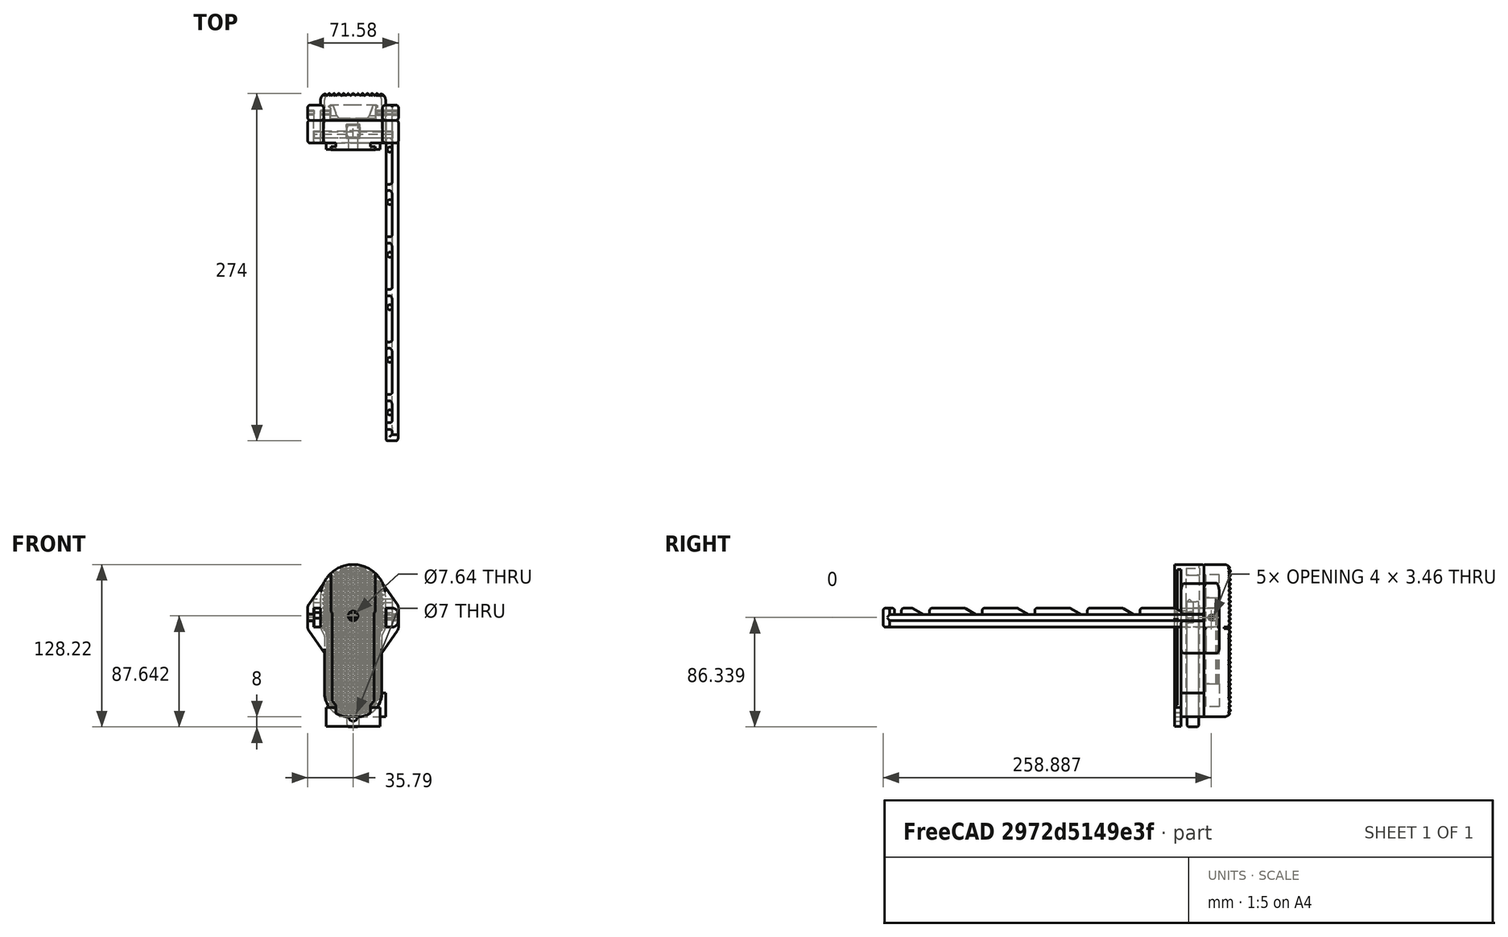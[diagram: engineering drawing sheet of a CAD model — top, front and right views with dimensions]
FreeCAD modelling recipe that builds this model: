
FCSTD DOCUMENT  (FreeCAD 0.19R24291 (Git))
Label: TelescopingButtExtensionPlasticArmsV3
License: All rights reserved
LicenseURL: http://en.wikipedia.org/wiki/All_rights_reserved
objects: Sketcher::SketchObject×35, PartDesign::Pocket×17, PartDesign::Pad×15, PartDesign::Fillet×10, PartDesign::Body×9, Spreadsheet::Sheet×5, PartDesign::Mirrored×4, PartDesign::LinearPattern×3, App::Part×3, Part::Mirroring×2, PartDesign::SubtractivePipe×1, PartDesign::AdditivePipe×1, PartDesign::Groove×1, PartDesign::Chamfer×1
note: 145 computed .brp shape members not serialized (recipe doc carries the construction recipe); baked Part::Feature solids carry a one-line shape summary decoded from their .brp

FEATURE [Spreadsheet::Sheet] Spreadsheet  label="P90Measurements"
  cells = A1=ButtDovetail; D1=Overall; G1=ButtPad; I1=Reference Point; J1=Bottom of pad, just at base of dovetail body; L1=SpaceForTelescopingBar; M1(SpaceForTelescopingBar)==0.584"; A2=DovetailHeight; B2(DovetailHeight)==5mm; D2=ButtOverallHeight; E2(ButtOverallHeight)==4.733"; G2=PadWidestWidth; H2(PadWidestWidth)==2.017"; A3=DovetailBodyWidth; B3(DovetailBodyWidth)==28mm; D3=PadBCGHoleFromReferencePoint; E3(PadBCGHoleFromReferencePoint)==2.997"; G3=PadThinnestWidth; H3(PadThinnestWidth)==1.772"; A4=DovetailLedgeHeight; B4(DovetailLedgeHeight)==2.5mm; D4=PadBCGHoleDiameter; E4(PadBCGHoleDiameter)==0.277"; G4=PadWidestWidthInnerShoulderDistanceFromReferencePoint; H4(PadWidestWidthInnerShoulderDistanceFromReferencePoint)==2.532"; A5=DovetailLedgeWidestWidth; B5(DovetailLedgeWidestWidth)==35.5mm; D5=PadBCGHoleDepth; E5(PadBCGHoleDepth)==0.375"; G5=PadWidestWidthOuterShoulderDistanceFromReferencePoint; H5(PadWidestWidthOuterShoulderDistanceFromReferencePoint)==2.785"; A6=DovetailLedgeMiddleWidth; B6(DovetailLedgeMiddleWidth)==1.32"; G6=PadBottomWidth; H6(PadBottomWidth)==0.3"; A7=DovetailMiddleWidthInsideShoulderDistanceFromReferencePoint; B7(DovetailMiddleWidthInsideShoulderDistanceFromReferencePoint)==0.37"; A8=DovetailMiddleWidthOutsideShoulderDistanceFromReferencePoint; B8(DovetailMiddleWidthOutsideShoulderDistanceFromReferencePoint)==0.484"; A9=DovetailBottobBodyBevelDistanceFromReferencePoint; B9(DovetailBottobBodyBevelDistanceFromReferencePoint)==0.154"; A10=DovetailWidestLedgeStartingPointFromReferencePoint; B10(DovetailWidestLedgeStartingPointFromReferencePoint)==3.222"
FEATURE [Spreadsheet::Sheet] Spreadsheet001  label="ProjectSettings"
  cells = A1=Tolerance; A2=LooseTolerance; B2(LooseTolerance)==0.3mm; C2=SpringMaxHeight; D2(SpringMaxHeight)==20mm; E2=CrosspinWidth; F2(CrosspinWidth)==4mm; G2=EndcapScrewBodyDiameter; H2(EndcapScrewBodyDiameter)==4mm; I2=LengthFromButtToChargingHandleShelf; J2(LengthFromButtToChargingHandleShelf)==310mm; K2=AdditionalPrinterTolerance; L2(AdditionalPrinterTolerance)==0mm; A3=TightTolerance; B3(TightTolerance)==0.1mm + AdditionalPrinterTolerance; C3=TelescopingPadOAL; D3(TelescopingPadOAL)==TelescopingBarInsertDepth + TelescopingButtThickness; E3=CrosspinHeight; F3(CrosspinHeight)==BarHeight / 3; G3=EndcapScrewHeadDiameter; H3(EndcapScrewHeadDiameter)==6mm; K3=SupportGap; L3(SupportGap)==0.16mm; A4=WallThickness; B4(WallThickness)==4mm; C4=StandardFillet; D4(StandardFillet)==2mm; E4=CrosspinLength; G4=EndcapNutHeight; H4(EndcapNutHeight)==0.273"; A5=LockingButtonWidth; B5(LockingButtonWidth)==10mm; C5=LockingPinWidth; D5(LockingPinWidth)==0.1875"; E5=ButtonActuationDistance; F5(ButtonActuationDistance)==CrosspinHeight * 2; G5=EndcapNutThickness; H5(EndcapNutThickness)==0.121"; A6=LockingButtonHeight; B6(LockingButtonHeight)==10mm; C6=LockingPinHeight; D6(LockingPinHeight)==BarHeight / 3 - LooseTolerance * 2; G6=EndcapSectionOnBarLength; H6(EndcapSectionOnBarLength)==15mm; A7=LockingButtonLength; B7(LockingButtonLength)==60mm; C7=LockingPinLength; D7(LockingPinLength)==40mm; G7=EndcapSectionHangingOffOfBarLength; H7(EndcapSectionHangingOffOfBarLength)==WallThickness; A8=LockingButtonHoleDepth; B8(LockingButtonHoleDepth)==<<P90Measurements>>.PadWidestWidthOuterShoulderDistanceFromReferencePoint + BarThickness + LockingPinHeight * 3 + SpringMaxHeight; C8=BarThickness; D8(BarThickness)==5mm; G8=ScrewCountersinkDepth; H8(ScrewCountersinkDepth)==0.089"; A9=LockingButtonActuationDistance; B9(LockingButtonActuationDistance)==6mm; C9=BarHeight; D9(BarHeight)==15mm; G9=EndcapScrewThreadHeight; H9(EndcapScrewThreadHeight)==8mm; A10=LockingBodyLength; B10(LockingBodyLength)==WallThickness * 2 + LockingButtonHeight; C10=BarLength; D10(BarLength)==265mm; A11=TelescopingPadComfortFilletRadius; B11(TelescopingPadComfortFilletRadius)==5mm; C11=BarNumberOfKnotches; D11(BarNumberOfKnotches)=6; C12=TelescopingBarInsertDepth; D12(TelescopingBarInsertDepth)==WallThickness * 2 + CrosspinWidth; A13=ScallopRadius; B13(ScallopRadius)==1.5mm; C13=TelescopingButtThickness; D13(TelescopingButtThickness)==10mm; A14=DistanceBetweenScallops; B14(DistanceBetweenScallops)==0.25mm; C14=BarDistanceBetweenKnotches; D14(BarDistanceBetweenKnotches)=; C15=BarLastKnotchLocationFromOrigin; D15(BarLastKnotchLocationFromOrigin)==BarLength - EndcapSectionOnBarLength - WallThickness; A16=PaperworkLidNubWidth; B16(PaperworkLidNubWidth)==2mm; C16=BarOccupiedLength; D16(BarOccupiedLength)==WallThickness * 4 + LockingButtonHeight + CrosspinWidth; A17=PaperworkLidNubHeight; B17(PaperworkLidNubHeight)==1.5mm; C17=BarUnoccupiedLength; D17(BarUnoccupiedLength)==BarLength - BarOccupiedLength; A18=PaperworkLidWallThickness; B18(PaperworkLidWallThickness)==2mm; C18=BarRackAngle; D18(BarRackAngle)=150; A19=PaperworkLidFingerHoleDiameter; B19(PaperworkLidFingerHoleDiameter)==20mm; C19=BarRackFillet; D19(BarRackFillet)==2mm; A20=PaperworkLipTabWallFilletRadius; B20(PaperworkLipTabWallFilletRadius)==4mm; C20=BarFillet; D20(BarFillet)==2mm; A21=PaperwokLipInteriorWallAngle; B21(PaperwokLipInteriorWallAngle)=110; C21=BarRackStartOffset; D21(BarRackStartOffset)==TelescopingBarInsertDepth + WallThickness + LockingButtonWidth / 2; A22=PaperworklidbaseThickness; B22(PaperworklidbaseThickness)==1.5mm; C22=BarRackEndoffset; D22(BarRackEndoffset)==WallThickness * 2 + LockingPinWidth + BarThickness; C23=BarRackL:ength; D23(BarRackLength)==13.6mm; A24=LockingButtonHoleClearanceForChamfer; B24(LockingButtonHoleClearanceForChamfer)==min(LockingButtonWidth; LockingButtonHeight) * 9 / 20; C24=BarEndcapThickness; D24(BarEndcapThickness)==BarThickness; A25=LockingPinPocketOverhangCompensationDistance; B25(LockingPinPocketOverhangCompensationDistance)==1.5mm; C25=PadCrosspinLength; D25(PadCrosspinLength)==17mm; C26=BCGInsertOffset; D26(BCGInsertOffset)==5mm; A27=LockingBodyPadThickness; B27(LockingBodyPadThickness)==WallThickness * 2 + LockingButtonHeight; C27=BCGWidth; D27(BCGWidth)==42.5mm; C28=BcgEndHeight; D28(BcgEndHeight)==15mm
FEATURE [Sketcher::SketchObject] Sketch  label="DovetailBodySketch"
  FullyConstrained = true
  MapMode = 5
  Placement = pos=(0,0,0) rot=(1,0,0;1.5708rad)
  Support = -> [XZ_Plane]
  expr: Constraints[9] = <<P90Measurements>>.ButtOverallHeight
  expr: Constraints[10] = <<P90Measurements>>.DovetailBodyWidth - <<ProjectSettings>>.LooseTolerance * 2
  sketch-geometry (4):
    g0: LineSegment StartX=-13.7 StartY=120.218 StartZ=0 EndX=13.7 EndY=120.218 EndZ=0
    g1: LineSegment StartX=13.7 StartY=120.218 StartZ=0 EndX=13.7 EndY=0 EndZ=0
    g2: LineSegment StartX=13.7 StartY=0 StartZ=0 EndX=-13.7 EndY=0 EndZ=0
    g3: LineSegment StartX=-13.7 StartY=0 StartZ=0 EndX=-13.7 EndY=120.218 EndZ=0
  constraints (11):
    c: Coincident(g0,g1)
    c: Coincident(g1,g2)
    c: Coincident(g2,g3)
    c: Coincident(g3,g0)
    c: Horizontal(g0)
    c: Vertical(g1)
    c: Vertical(g3)
    c: PointOnObject(g1,g-1)
    c: Symmetric(g1,g2,g-2)
    c: DistanceY(g1,g1) = 120.218
    c: DistanceX(g0,g0) = 27.4
FEATURE [PartDesign::Pad] Pad  label="DovetailBodyPad"
  Direction = (1,1,1)
  Length = 5.2
  Length2 = 100
  Placement = pos=(0,0,0) rot=(1,0,0;1.5708rad)
  Profile = -> Sketch
  Type = 0
  expr: Length = <<P90Measurements>>.DovetailHeight + <<ProjectSettings>>.TightTolerance * 2
FEATURE [Sketcher::SketchObject] Sketch001  label="DovetailLedgeSketch"
  AttachmentOffset = pos=(0,0,5.2) rot=(0,0,1;0rad)
  FullyConstrained = true
  MapMode = 5
  Placement = pos=(0,-5.2,-1.2e-15) rot=(1,0,0;1.5708rad)
  Support = -> [XZ_Plane]
  expr: Constraints[9] = <<P90Measurements>>.ButtOverallHeight
  expr: Constraints[10] = <<P90Measurements>>.DovetailLedgeWidestWidth - <<ProjectSettings>>.LooseTolerance * 2
  expr: .AttachmentOffset.Base.z = <<DovetailBodyPad>>.Length
  sketch-geometry (4):
    g0: LineSegment StartX=-17.45 StartY=120.218 StartZ=0 EndX=17.45 EndY=120.218 EndZ=0
    g1: LineSegment StartX=17.45 StartY=120.218 StartZ=0 EndX=17.45 EndY=0 EndZ=0
    g2: LineSegment StartX=17.45 StartY=0 StartZ=0 EndX=-17.45 EndY=0 EndZ=0
    g3: LineSegment StartX=-17.45 StartY=0 StartZ=0 EndX=-17.45 EndY=120.218 EndZ=0
  constraints (11):
    c: Coincident(g0,g1)
    c: Coincident(g1,g2)
    c: Coincident(g2,g3)
    c: Coincident(g3,g0)
    c: Horizontal(g0)
    c: Vertical(g1)
    c: Vertical(g3)
    c: PointOnObject(g1,g-1)
    c: Symmetric(g2,g1,g-2)
    c: DistanceY(g1,g1) = 120.218
    c: DistanceX(g0,g0) = 34.9
FEATURE [PartDesign::Pad] Pad001  label="DovetailLedgePad"
  BaseFeature = -> Pad
  Direction = (1,1,1)
  Length = 2.3
  Length2 = 100
  Placement = pos=(0,0,0) rot=(1,0,0;1.5708rad)
  Profile = -> Sketch001
  Refine = true
  Reversed = true
  Type = 0
  expr: Length = <<P90Measurements>>.DovetailLedgeHeight - <<ProjectSettings>>.TightTolerance * 2
FEATURE [Sketcher::SketchObject] Sketch002  label="DovetailLedgeCutSketch"
  FullyConstrained = true
  MapMode = 5
  Placement = pos=(0,0,0) rot=(1,0,0;1.5708rad)
  Support = -> [XZ_Plane]
  expr: Constraints[28] = <<P90Measurements>>.ButtOverallHeight
  expr: Constraints[29] = <<P90Measurements>>.DovetailLedgeWidestWidth - <<ProjectSettings>>.LooseTolerance * 2
  expr: Constraints[32] = <<P90Measurements>>.DovetailBodyWidth - <<ProjectSettings>>.LooseTolerance * 2
  expr: Constraints[34] = <<P90Measurements>>.DovetailMiddleWidthInsideShoulderDistanceFromReferencePoint
  expr: Constraints[36] = <<P90Measurements>>.DovetailWidestLedgeStartingPointFromReferencePoint
  expr: Constraints[33] = <<P90Measurements>>.DovetailLedgeMiddleWidth - <<ProjectSettings>>.LooseTolerance * 2
  expr: Constraints[35] = <<P90Measurements>>.DovetailMiddleWidthOutsideShoulderDistanceFromReferencePoint
  sketch-geometry (16):
    g0: LineSegment StartX=-27.45 StartY=130.218 StartZ=0 EndX=27.45 EndY=130.218 EndZ=0
    g1: LineSegment StartX=27.45 StartY=130.218 StartZ=0 EndX=27.45 EndY=-10 EndZ=0
    g2: LineSegment StartX=27.45 StartY=-10 StartZ=0 EndX=-27.45 EndY=-10 EndZ=0
    g3: LineSegment StartX=-27.45 StartY=-10 StartZ=0 EndX=-27.45 EndY=130.218 EndZ=0
    g4: LineSegment StartX=-13.7 StartY=0 StartZ=0 EndX=13.7 EndY=0 EndZ=0
    g5: LineSegment StartX=13.7 StartY=0 StartZ=0 EndX=13.7 EndY=9.398 EndZ=0
    g6: LineSegment StartX=13.7 StartY=9.398 StartZ=0 EndX=16.464 EndY=12.2936 EndZ=0
    g7: LineSegment StartX=16.464 StartY=12.2936 StartZ=0 EndX=16.464 EndY=81.8388 EndZ=0
    g8: LineSegment StartX=16.464 StartY=81.8388 StartZ=0 EndX=17.45 EndY=82.8598 EndZ=0
    g9: LineSegment StartX=17.45 StartY=82.8598 StartZ=0 EndX=17.45 EndY=120.218 EndZ=0
    g10: LineSegment StartX=17.45 StartY=120.218 StartZ=0 EndX=-17.45 EndY=120.218 EndZ=0
    g11: LineSegment StartX=-17.45 StartY=120.218 StartZ=0 EndX=-17.45 EndY=82.8598 EndZ=0
    g12: LineSegment StartX=-17.45 StartY=82.8598 StartZ=0 EndX=-16.464 EndY=81.8388 EndZ=0
    g13: LineSegment StartX=-16.464 StartY=81.8388 StartZ=0 EndX=-16.464 EndY=12.2936 EndZ=0
    g14: LineSegment StartX=-16.464 StartY=12.2936 StartZ=0 EndX=-13.7 EndY=9.398 EndZ=0
    g15: LineSegment StartX=-13.7 StartY=9.398 StartZ=0 EndX=-13.7 EndY=0 EndZ=0
  constraints (44):
    c: Coincident(g0,g1)
    c: Coincident(g1,g2)
    c: Coincident(g2,g3)
    c: Coincident(g3,g0)
    c: Horizontal(g0)
    c: Horizontal(g2)
    c: Vertical(g1)
    c: Vertical(g3)
    c: PointOnObject(g4,g-1)
    c: Coincident(g4,g5)
    c: Vertical(g5)
    c: Coincident(g5,g6)
    c: Coincident(g6,g7)
    c: Vertical(g7)
    c: Coincident(g7,g8)
    c: Coincident(g8,g9)
    c: Vertical(g9)
    c: Coincident(g9,g10)
    c: Coincident(g10,g11)
    c: Coincident(g11,g12)
    c: Coincident(g12,g13)
    c: Vertical(g13)
    c: Coincident(g13,g14)
    c: Coincident(g14,g15)
    c: Coincident(g15,g4)
    c: Vertical(g15)
    c: Horizontal(g14,g5)
    c: Horizontal(g13,g6)
    c: DistanceY(g4,g9) = 120.218
    c: DistanceX(g10,g10) = 34.9
    c: Symmetric(g10,g9,g-2)
    c: Symmetric(g12,g7,g-2)
    c: DistanceX(g4,g4) = 27.4
    c: DistanceX(g12,g7) = 32.928
    c: DistanceY(g14) = 9.398
    c: DistanceY(g4,g13) = 12.2936
    c: DistanceY(g-1,g7) = 81.8388
    c: DistanceY(g10,g0) = 10
    c: DistanceX(g0,g10) = 10
    c: DistanceX(g9,g1) = 10
    c: DistanceY(g1,g4) = 10
    c: Symmetric(g4,g4,g-2)
    c: Symmetric(g8,g11,g-2)
    c: Angle(g12,g13) = 2.37365
FEATURE [PartDesign::Pocket] Pocket  label="DovetailLedgeCutPocket"
  BaseFeature = -> Pad001
  Length = 5
  Length2 = 100
  Placement = pos=(0,0,0) rot=(1,0,0;1.5708rad)
  Profile = -> Sketch002
  Reversed = true
  Type = 1
FEATURE [Sketcher::SketchObject] Sketch003  label="PadBodySketch"
  FullyConstrained = true
  MapMode = 5
  Placement = pos=(0,0,0) rot=(1,0,0;1.5708rad)
  Support = -> [XZ_Plane]
  expr: Constraints[20] = <<P90Measurements>>.ButtOverallHeight
  expr: Constraints[21] = <<P90Measurements>>.PadWidestWidth
  expr: Constraints[19] = <<P90Measurements>>.PadThinnestWidth
  expr: Constraints[22] = <<P90Measurements>>.PadWidestWidthOuterShoulderDistanceFromReferencePoint
  expr: Constraints[27] = <<P90Measurements>>.PadWidestWidthInnerShoulderDistanceFromReferencePoint
  sketch-geometry (12):
    g0: LineSegment StartX=-22.5044 StartY=0 StartZ=0 EndX=22.5044 EndY=0 EndZ=0
    g1: LineSegment StartX=22.5044 StartY=0 StartZ=0 EndX=22.5044 EndY=63.2152 EndZ=0
    g2: LineSegment StartX=-22.5044 StartY=63.2152 StartZ=0 EndX=-22.5044 EndY=0 EndZ=0
    g3: LineSegment StartX=-25.6159 StartY=120.218 StartZ=0 EndX=25.6159 EndY=120.218 EndZ=0
    g4: LineSegment StartX=25.6159 StartY=120.218 StartZ=0 EndX=25.6159 EndY=70.739 EndZ=0
    g5: LineSegment StartX=-25.6159 StartY=70.739 StartZ=0 EndX=-25.6159 EndY=120.218 EndZ=0
    g6: LineSegment StartX=-25.3621 StartY=69.6414 StartZ=0 EndX=-22.7582 EndY=64.3128 EndZ=0
    g7: LineSegment StartX=25.3621 StartY=69.6414 StartZ=0 EndX=22.7582 EndY=64.3128 EndZ=0
    g8: ArcOfCircle CenterX=-23.1159 CenterY=70.739 CenterZ=0 NormalX=0 NormalY=0 NormalZ=1 AngleXU=0 Radius=2.5 StartAngle=3.14159 EndAngle=3.59612
    g9: ArcOfCircle CenterX=-25.0044 CenterY=63.2152 CenterZ=0 NormalX=0 NormalY=0 NormalZ=1 AngleXU=0 Radius=2.5 StartAngle=2e-16 EndAngle=0.454529
    g10: ArcOfCircle CenterX=23.1159 CenterY=70.739 CenterZ=0 NormalX=0 NormalY=0 NormalZ=1 AngleXU=0 Radius=2.5 StartAngle=5.82866 EndAngle=6.28319
    g11: ArcOfCircle CenterX=25.0044 CenterY=63.2152 CenterZ=0 NormalX=0 NormalY=0 NormalZ=1 AngleXU=0 Radius=2.5 StartAngle=2.68706 EndAngle=3.14159
  constraints (28):
    c: Coincident(g0,g1)
    c: Coincident(g2,g0)
    c: Vertical(g1)
    c: Vertical(g2)
    c: PointOnObject(g0,g-1)
    c: Coincident(g3,g4)
    c: Coincident(g5,g3)
    c: Vertical(g4)
    c: Vertical(g5)
    c: Tangent(g8,g5) = 1.5708
    c: Tangent(g8,g6) = -1.5708
    c: Tangent(g9,g6) = 1.5708
    c: Tangent(g11,g1) = 1.5708
    c: Tangent(g11,g7) = -1.5708
    c: Tangent(g7,g10) = 1.5708
    c: Tangent(g10,g4) = 1.5708
    c: Tangent(g9,g2) = 1.5708
    c: Symmetric(g0,g0,g-2)
    c: Symmetric(g3,g3,g-2)
    c: DistanceX(g0,g0) = 45.0088
    c: DistanceY(g0,g3) = 120.218
    c: DistanceX(g3,g3) = 51.2318
    c: DistanceY(g-1,g8) = 70.739
    c: Symmetric(g7,g6,g-2)
    c: Symmetric(g6,g7,g-2)
    c: Equal(g11,g10)
    c: Diameter(g11) = 5
    c: DistanceY(g6) = 64.3128
FEATURE [PartDesign::Pad] Pad002  label="PadBodyPad"
  BaseFeature = -> Pocket
  Direction = (1,1,1)
  Length = 18
  Length2 = 100
  Placement = pos=(0,0,0) rot=(1,0,0;1.5708rad)
  Profile = -> Sketch003
  Reversed = true
  Type = 0
  expr: Length = <<ProjectSettings>>.LockingBodyPadThickness
FEATURE [Sketcher::SketchObject] Sketch004  label="PadBevelsCutSketch"
  FullyConstrained = true
  MapMode = 5
  Placement = pos=(0,0,0) rot=(1,0,0;1.5708rad)
  Support = -> [XZ_Plane]
  expr: Constraints[27] = <<P90Measurements>>.ButtOverallHeight
  expr: Constraints[30] = <<P90Measurements>>.PadThinnestWidth
  expr: Constraints[31] = <<P90Measurements>>.PadWidestWidthInnerShoulderDistanceFromReferencePoint - 5mm
  expr: Constraints[29] = <<P90Measurements>>.PadWidestWidth
  expr: Constraints[32] = <<P90Measurements>>.PadBottomWidth
  sketch-geometry (15):
    g0: LineSegment StartX=-35.6159 StartY=130.218 StartZ=0 EndX=35.6159 EndY=130.218 EndZ=0
    g1: LineSegment StartX=35.6159 StartY=130.218 StartZ=0 EndX=35.6159 EndY=-10 EndZ=0
    g2: LineSegment StartX=35.6159 StartY=-10 StartZ=0 EndX=-35.6159 EndY=-10 EndZ=0
    g3: LineSegment StartX=-35.6159 StartY=-10 StartZ=0 EndX=-35.6159 EndY=130.218 EndZ=0
    g4: ArcOfCircle CenterX=-3.81 CenterY=18.6944 CenterZ=0 NormalX=0 NormalY=0 NormalZ=1 AngleXU=0 Radius=18.6944 StartAngle=3.14159 EndAngle=4.71239
    g5: ArcOfCircle CenterX=3.81 CenterY=18.6944 CenterZ=0 NormalX=0 NormalY=0 NormalZ=1 AngleXU=0 Radius=18.6944 StartAngle=4.71239 EndAngle=6.28319
    g6: ArcOfCircle CenterX=2.5e-15 CenterY=94.6023 CenterZ=0 NormalX=0 NormalY=0 NormalZ=1 AngleXU=0 Radius=25.6159 StartAngle=1.5708 EndAngle=3.14159
    g7: ArcOfCircle CenterX=2.5e-15 CenterY=94.6023 CenterZ=0 NormalX=0 NormalY=0 NormalZ=1 AngleXU=0 Radius=25.6159 StartAngle=0 EndAngle=1.5708
    g8: LineSegment StartX=-25.6159 StartY=94.6023 StartZ=0 EndX=-25.6159 EndY=59.3128 EndZ=0
    g9: LineSegment StartX=-25.6159 StartY=59.3128 StartZ=0 EndX=-22.5044 EndY=59.3128 EndZ=0
    g10: LineSegment StartX=-22.5044 StartY=59.3128 StartZ=0 EndX=-22.5044 EndY=18.6944 EndZ=0
    g11: LineSegment StartX=-3.81 StartY=0 StartZ=0 EndX=3.81 EndY=0 EndZ=0
    g12: LineSegment StartX=22.5044 StartY=18.6944 StartZ=0 EndX=22.5044 EndY=59.3128 EndZ=0
    g13: LineSegment StartX=22.5044 StartY=59.3128 StartZ=0 EndX=25.6159 EndY=59.3128 EndZ=0
    g14: LineSegment StartX=25.6159 StartY=59.3128 StartZ=0 EndX=25.6159 EndY=94.6023 EndZ=0
  constraints (39):
    c: Coincident(g0,g1)
    c: Coincident(g1,g2)
    c: Coincident(g2,g3)
    c: Coincident(g3,g0)
    c: Horizontal(g0)
    c: Vertical(g1)
    c: Vertical(g3)
    c: Symmetric(g2,g1,g-2)
    c: PointOnObject(g4,g-1)
    c: PointOnObject(g5,g-1)
    c: Vertical(g8)
    c: Coincident(g9,g8)
    c: Vertical(g10)
    c: Vertical(g12)
    c: Coincident(g13,g12)
    c: Vertical(g14)
    c: Coincident(g13,g14)
    c: Horizontal(g13)
    c: Tangent(g6,g8) = -1.5708
    c: Tangent(g7,g14) = -1.5708
    c: Tangent(g10,g4) = -1.5708
    c: Tangent(g11,g4) = -1.5708
    c: Tangent(g11,g5) = -1.5708
    c: Tangent(g12,g5) = -1.5708
    c: Symmetric(g12,g10,g-2)
    c: Symmetric(g8,g13,g-2)
    c: Coincident(g10,g9)
    c: DistanceY(g-1,g7) = 120.218
    c: Equal(g5,g4)
    c: DistanceX(g6,g7) = 51.2318
    c: DistanceX(g9,g12) = 45.0088
    c: DistanceY(g-1,g12) = 59.3128
    c: DistanceX(g11,g11) = 7.62
    c: PointOnObject(g6,g-2)
    c: Tangent(g6,g7) = -1.5708
    c: Equal(g8,g14)
    c: DistanceY(g2,g-1) = 10
    c: DistanceY(g6,g0) = 10
    c: DistanceX(g7,g1) = 10
FEATURE [PartDesign::Pocket] Pocket001  label="PadBevelsCutPocket"
  BaseFeature = -> Pad002
  Length = 5
  Length2 = 100
  Midplane = true
  Placement = pos=(0,0,0) rot=(1,0,0;1.5708rad)
  Profile = -> Sketch004
  Type = 1
FEATURE [Spreadsheet::Sheet] Spreadsheet002  label="TelescopingBarSettings"
  cells = A1=BarOffsetFromCenter; B1(BarOffsetFromCenter)==<<PadBodyPad>>.Length + <<TelescoptingPadBodyPad>>.Length; A2=LengthFromButtToChargingHandleShelf; B2(LengthFromButtToChargingHandleShelf)==310mm; A3=BarLength; B3(BarLength)==270mm; A4=BarThickness; B4(BarThickness)==0.125"; A5=CrosspinThickness; B5(CrosspinThickness)==0.125"; A6=BarHeight; B6(BarHeight)==12.7mm; A7=LockingPinThickness; B7(LockingPinThickness)==0.125"; A8=BarNumberOfKnotches; B8(BarNumberOfKnotches)=6; A9=ScrewCountersinkDepth; B9(ScrewCountersinkDepth)==0.089"; A10=EndcapHexnutHeight; B10(EndcapHexnutHeight)==0.273"; A11=EndcapHexnutThickness; B11(EndcapHexnutThickness)==0.121"; A12=CrosspinHeight; B12(CrosspinHeight)==6mm; A13=LockingPinHeight; B13(LockingPinHeight)==6mm
FEATURE [Sketcher::SketchObject] Sketch008  label="TelescoptingPadBodySketch"
  FullyConstrained = true
  MapMode = 5
  Placement = pos=(0,0,0) rot=(1,0,0;1.5708rad)
  Support = -> [XZ_Plane002]
  expr: Constraints[27] = <<P90Measurements>>.PadWidestWidthInnerShoulderDistanceFromReferencePoint
  expr: Constraints[22] = <<P90Measurements>>.PadWidestWidthOuterShoulderDistanceFromReferencePoint
  expr: Constraints[19] = <<P90Measurements>>.PadThinnestWidth
  expr: Constraints[21] = <<P90Measurements>>.PadWidestWidth
  expr: Constraints[20] = <<P90Measurements>>.ButtOverallHeight
  sketch-geometry (12):
    g0: LineSegment StartX=-22.5044 StartY=0 StartZ=0 EndX=22.5044 EndY=0 EndZ=0
    g1: LineSegment StartX=22.5044 StartY=0 StartZ=0 EndX=22.5044 EndY=63.2152 EndZ=0
    g2: LineSegment StartX=-22.5044 StartY=63.2152 StartZ=0 EndX=-22.5044 EndY=0 EndZ=0
    g3: LineSegment StartX=-25.6159 StartY=120.218 StartZ=0 EndX=25.6159 EndY=120.218 EndZ=0
    g4: LineSegment StartX=25.6159 StartY=120.218 StartZ=0 EndX=25.6159 EndY=70.739 EndZ=0
    g5: LineSegment StartX=-25.6159 StartY=70.739 StartZ=0 EndX=-25.6159 EndY=120.218 EndZ=0
    g6: LineSegment StartX=-25.3621 StartY=69.6414 StartZ=0 EndX=-22.7582 EndY=64.3128 EndZ=0
    g7: LineSegment StartX=25.3621 StartY=69.6414 StartZ=0 EndX=22.7582 EndY=64.3128 EndZ=0
    g8: ArcOfCircle CenterX=-23.1159 CenterY=70.739 CenterZ=0 NormalX=0 NormalY=0 NormalZ=1 AngleXU=0 Radius=2.5 StartAngle=3.14159 EndAngle=3.59612
    g9: ArcOfCircle CenterX=-25.0044 CenterY=63.2152 CenterZ=0 NormalX=0 NormalY=0 NormalZ=1 AngleXU=0 Radius=2.5 StartAngle=0 EndAngle=0.454529
    g10: ArcOfCircle CenterX=23.1159 CenterY=70.739 CenterZ=0 NormalX=0 NormalY=0 NormalZ=1 AngleXU=0 Radius=2.5 StartAngle=5.82866 EndAngle=6.28319
    g11: ArcOfCircle CenterX=25.0044 CenterY=63.2152 CenterZ=0 NormalX=0 NormalY=0 NormalZ=1 AngleXU=0 Radius=2.5 StartAngle=2.68706 EndAngle=3.14159
  constraints (29):
    c: Coincident(g0,g1)
    c: Coincident(g2,g0)
    c: Vertical(g1)
    c: Vertical(g2)
    c: PointOnObject(g0,g-1)
    c: Coincident(g3,g4)
    c: Coincident(g5,g3)
    c: Vertical(g4)
    c: Vertical(g5)
    c: Tangent(g8,g5) = 1.5708
    c: Tangent(g8,g6) = -1.5708
    c: Tangent(g9,g6) = 1.5708
    c: Tangent(g11,g1) = 1.5708
    c: Tangent(g11,g7) = -1.5708
    c: Tangent(g7,g10) = 1.5708
    c: Tangent(g10,g4) = 1.5708
    c: Tangent(g9,g2) = 1.5708
    c: Symmetric(g0,g0,g-2)
    c: Symmetric(g3,g3,g-2)
    c: DistanceX(g0,g0) = 45.0088
    c: DistanceY(g0,g3) = 120.218
    c: DistanceX(g3,g3) = 51.2318
    c: DistanceY(g-1,g8) = 70.739
    c: Symmetric(g7,g6,g-2)
    c: Symmetric(g6,g7,g-2)
    c: Equal(g11,g10)
    c: Diameter(g11) = 5
    c: DistanceY(g6) = 64.3128
    c: Angle(g1,g7) = 2.68706  'PadAngle'
FEATURE [PartDesign::Pad] Pad006  label="TelescoptingPadBodyPad"
  Direction = (1,1,1)
  Length = 21
  Length2 = 100
  Placement = pos=(0,0,0) rot=(1,0,0;1.5708rad)
  Profile = -> Sketch008
  Reversed = true
  Type = 0
  expr: Length = <<ProjectSettings>>.TelescopingBarInsertDepth + <<ProjectSettings>>.WallThickness + <<ProjectSettings>>.TelescopingPadComfortFilletRadius
FEATURE [Sketcher::SketchObject] Sketch009  label="TelescopingPadBevelsCutSketch"
  FullyConstrained = true
  MapMode = 5
  Placement = pos=(0,0,0) rot=(1,0,0;1.5708rad)
  Support = -> [XZ_Plane002]
  expr: Constraints[32] = <<P90Measurements>>.PadBottomWidth
  expr: Constraints[29] = <<P90Measurements>>.PadWidestWidth
  expr: Constraints[31] = <<P90Measurements>>.PadWidestWidthInnerShoulderDistanceFromReferencePoint - 5mm
  expr: Constraints[30] = <<P90Measurements>>.PadThinnestWidth
  expr: Constraints[27] = <<P90Measurements>>.ButtOverallHeight
  sketch-geometry (15):
    g0: LineSegment StartX=-35.6159 StartY=130.218 StartZ=0 EndX=35.6159 EndY=130.218 EndZ=0
    g1: LineSegment StartX=35.6159 StartY=130.218 StartZ=0 EndX=35.6159 EndY=-10 EndZ=0
    g2: LineSegment StartX=35.6159 StartY=-10 StartZ=0 EndX=-35.6159 EndY=-10 EndZ=0
    g3: LineSegment StartX=-35.6159 StartY=-10 StartZ=0 EndX=-35.6159 EndY=130.218 EndZ=0
    g4: ArcOfCircle CenterX=-3.81 CenterY=18.6944 CenterZ=0 NormalX=0 NormalY=0 NormalZ=1 AngleXU=0 Radius=18.6944 StartAngle=3.14159 EndAngle=4.71239
    g5: ArcOfCircle CenterX=3.81 CenterY=18.6944 CenterZ=0 NormalX=0 NormalY=0 NormalZ=1 AngleXU=0 Radius=18.6944 StartAngle=4.71239 EndAngle=6.28319
    g6: ArcOfCircle CenterX=8e-16 CenterY=94.6023 CenterZ=0 NormalX=0 NormalY=0 NormalZ=1 AngleXU=0 Radius=25.6159 StartAngle=1.5708 EndAngle=3.14159
    g7: ArcOfCircle CenterX=8e-16 CenterY=94.6023 CenterZ=0 NormalX=0 NormalY=0 NormalZ=1 AngleXU=0 Radius=25.6159 StartAngle=0 EndAngle=1.5708
    g8: LineSegment StartX=-25.6159 StartY=94.6023 StartZ=0 EndX=-25.6159 EndY=59.3128 EndZ=0
    g9: LineSegment StartX=-25.6159 StartY=59.3128 StartZ=0 EndX=-22.5044 EndY=59.3128 EndZ=0
    g10: LineSegment StartX=-22.5044 StartY=59.3128 StartZ=0 EndX=-22.5044 EndY=18.6944 EndZ=0
    g11: LineSegment StartX=-3.81 StartY=0 StartZ=0 EndX=3.81 EndY=0 EndZ=0
    g12: LineSegment StartX=22.5044 StartY=18.6944 StartZ=0 EndX=22.5044 EndY=59.3128 EndZ=0
    g13: LineSegment StartX=22.5044 StartY=59.3128 StartZ=0 EndX=25.6159 EndY=59.3128 EndZ=0
    g14: LineSegment StartX=25.6159 StartY=59.3128 StartZ=0 EndX=25.6159 EndY=94.6023 EndZ=0
  constraints (39):
    c: Coincident(g0,g1)
    c: Coincident(g1,g2)
    c: Coincident(g2,g3)
    c: Coincident(g3,g0)
    c: Horizontal(g0)
    c: Vertical(g1)
    c: Vertical(g3)
    c: Symmetric(g2,g1,g-2)
    c: PointOnObject(g4,g-1)
    c: PointOnObject(g5,g-1)
    c: Vertical(g8)
    c: Coincident(g9,g8)
    c: Vertical(g10)
    c: Vertical(g12)
    c: Coincident(g13,g12)
    c: Vertical(g14)
    c: Coincident(g13,g14)
    c: Horizontal(g13)
    c: Tangent(g6,g8) = -1.5708
    c: Tangent(g7,g14) = -1.5708
    c: Tangent(g10,g4) = -1.5708
    c: Tangent(g11,g4) = -1.5708
    c: Tangent(g11,g5) = -1.5708
    c: Tangent(g12,g5) = -1.5708
    c: Symmetric(g12,g10,g-2)
    c: Symmetric(g8,g13,g-2)
    c: Coincident(g10,g9)
    c: DistanceY(g-1,g7) = 120.218
    c: Equal(g5,g4)
    c: DistanceX(g6,g7) = 51.2318
    c: DistanceX(g9,g12) = 45.0088
    c: DistanceY(g-1,g12) = 59.3128
    c: DistanceX(g11,g11) = 7.62
    c: PointOnObject(g6,g-2)
    c: Tangent(g6,g7) = -1.5708
    c: Equal(g8,g14)
    c: DistanceY(g2,g-1) = 10
    c: DistanceY(g6,g0) = 10
    c: DistanceX(g7,g1) = 10
FEATURE [PartDesign::Pocket] Pocket002  label="TelescopingPadBevelsCutPocket"
  BaseFeature = -> Pad006
  Length = 5
  Length2 = 100
  Midplane = true
  Placement = pos=(0,0,0) rot=(1,0,0;1.5708rad)
  Profile = -> Sketch009
  Type = 1
FEATURE [Sketcher::SketchObject] Sketch010  label="TelescopingBarInsertArmSketch"
  FullyConstrained = true
  MapMode = 5
  Placement = pos=(0,0,0) rot=(1,0,0;1.5708rad)
  Support = -> [XZ_Plane002]
  expr: Constraints[27] = <<ProjectSettings>>.BarThickness + <<ProjectSettings>>.TightTolerance * 2
  expr: Constraints[9] = <<ProjectSettings>>.BarThickness + <<ProjectSettings>>.LooseTolerance * 2
  expr: Constraints[10] = <<P90Measurements>>.PadWidestWidthOuterShoulderDistanceFromReferencePoint
  expr: Constraints[8] = <<P90Measurements>>.PadWidestWidth / 2
  expr: Constraints[13] = <<P90Measurements>>.PadThinnestWidth / 2
  expr: Constraints[11] = <<ProjectSettings>>.BarHeight + <<ProjectSettings>>.TightTolerance * 2
  sketch-geometry (13):
    g0: LineSegment StartX=31.2159 StartY=70.739 StartZ=0 EndX=31.2159 EndY=85.939 EndZ=0
    g1: LineSegment StartX=30.8159 StartY=85.939 StartZ=0 EndX=25.6159 EndY=85.939 EndZ=0
    g2: LineSegment StartX=25.6159 StartY=85.939 StartZ=0 EndX=25.6159 EndY=70.739 EndZ=0
    g3: LineSegment StartX=25.6159 StartY=70.739 StartZ=0 EndX=30.8159 EndY=70.739 EndZ=0
    g4: LineSegment StartX=35.7859 StartY=70.739 StartZ=0 EndX=35.7859 EndY=86.039 EndZ=0
    g5: LineSegment StartX=22.5044 StartY=106.448 StartZ=0 EndX=22.5044 EndY=50.3301 EndZ=0
    g6: ArcOfCircle CenterX=31.2159 CenterY=70.739 CenterZ=0 NormalX=0 NormalY=0 NormalZ=1 AngleXU=0 Radius=4.57 StartAngle=5.67232 EndAngle=6.28319
    g7: LineSegment StartX=22.5044 StartY=50.3301 StartZ=0 EndX=34.9594 EndY=68.1178 EndZ=0
    g8: LineSegment StartX=22.5044 StartY=106.448 StartZ=0 EndX=34.9594 EndY=88.6602 EndZ=0
    g9: ArcOfCircle CenterX=31.2159 CenterY=86.039 CenterZ=0 NormalX=0 NormalY=0 NormalZ=1 AngleXU=0 Radius=4.57 StartAngle=4e-16 EndAngle=0.610865
    g10: LineSegment StartX=30.8159 StartY=85.939 StartZ=0 EndX=30.8159 EndY=70.739 EndZ=0
    g11: LineSegment StartX=30.8159 StartY=70.739 StartZ=0 EndX=31.2159 EndY=70.739 EndZ=0
    g12: LineSegment StartX=30.8159 StartY=85.939 StartZ=0 EndX=31.2159 EndY=85.939 EndZ=0
  constraints (36):
    c: Vertical(g0)
    c: Horizontal(g1)
    c: Coincident(g1,g2)
    c: Vertical(g2)
    c: Coincident(g2,g3)
    c: Vertical(g5)
    c: Vertical(g4)
    c: Horizontal(g3)
    c: DistanceX(g-1,g2) = 25.6159
    c: DistanceX(g1,g0) = 5.6
    c: DistanceY(g-1,g2) = 70.739
    c: DistanceY(g0,g0) = 15.2
    c: Coincident(g6,g0)
    c: DistanceX(g-1,g5) = 22.5044
    c: Coincident(g7,g5)
    c: Coincident(g8,g5)
    c: Tangent(g6,g4) = -1.5708
    c: Tangent(g7,g6) = -1.5708
    c: Equal(g7,g8)
    c: Angle(g4,g7) = 2.53073
    c: DistanceX(g-1,g4) = 35.7859  'DistanceFromCenterlineToOutsideOfBarInsertArm'
    c: PointOnObject(g9,g0)
    c: DistanceY(g0,g9) = 0.1
    c: Tangent(g9,g8) = 1.5708
    c: Tangent(g9,g4) = -1.5708
    c: Diameter(g9) = 9.14
    c: Vertical(g10)
    c: DistanceX(g1,g10) = 5.2
    c: Coincident(g1,g10)
    c: Coincident(g3,g10)
    c: Coincident(g11,g3)
    c: Coincident(g11,g6)
    c: Coincident(g12,g1)
    c: Coincident(g12,g0)
    c: Horizontal(g12)
    c: Horizontal(g11)
FEATURE [Spreadsheet::Sheet] Spreadsheet003  label="TelescopingPadSettings"
  cells = A1=TelescopingBarInsertDepth; B1(TelescopingBarInsertDepth)==<<ProjectSettings>>.WallThickness * 2 + <<TelescopingBarSettings>>.CrosspinThickness + <<ProjectSettings>>.TightTolerance * 2; A2=TelescopingButtThickness; B2(TelescopingButtThickness)==10mm; A3=TelescopingPadOAL; B3(TelescopingPadOAL)==TelescopingBarInsertDepth + TelescopingButtThickness
FEATURE [PartDesign::Pad] Pad007  label="TelescopingBarInsertArmPad"
  BaseFeature = -> Pocket002
  Direction = (1,1,1)
  Length = 12
  Length2 = 100
  Placement = pos=(0,0,0) rot=(1,0,0;1.5708rad)
  Profile = -> Sketch010
  Reversed = true
  Type = 0
  expr: Length = <<ProjectSettings>>.TelescopingBarInsertDepth
FEATURE [Sketcher::SketchObject] Sketch011  label="CrosspinHoleSketch"
  FullyConstrained = true
  MapMode = 5
  Placement = pos=(0,0,0) rot=(0.57735,0.57735,0.57735;2.0944rad)
  Support = -> [YZ_Plane002]
  expr: Constraints[1] = <<TelescopingPadSettings>>.TelescopingBarInsertDepth / 2 + <<ProjectSettings>>.TightTolerance * 2
  expr: Constraints[0] = <<P90Measurements>>.PadWidestWidthOuterShoulderDistanceFromReferencePoint + <<ProjectSettings>>.BarHeight / 2 + <<ProjectSettings>>.TightTolerance
  expr: Constraints[2] = <<ProjectSettings>>.CrosspinWidth
  sketch-geometry (8):
    g0: Circle CenterX=5.8875 CenterY=78.339 CenterZ=0 NormalX=0 NormalY=0 NormalZ=1 AngleXU=0 Radius=2
    g1: LineSegment StartX=4.8875 StartY=80.0711 StartZ=0 EndX=3.8875 EndY=78.339 EndZ=0
    g2: LineSegment StartX=3.8875 StartY=78.339 StartZ=0 EndX=4.8875 EndY=76.6069 EndZ=0
    g3: LineSegment StartX=4.8875 StartY=76.6069 StartZ=0 EndX=6.8875 EndY=76.6069 EndZ=0
    g4: LineSegment StartX=6.8875 StartY=76.6069 StartZ=0 EndX=7.8875 EndY=78.339 EndZ=0
    g5: LineSegment StartX=7.8875 StartY=78.339 StartZ=0 EndX=6.8875 EndY=80.0711 EndZ=0
    g6: LineSegment StartX=6.8875 StartY=80.0711 StartZ=0 EndX=4.8875 EndY=80.0711 EndZ=0
    g7: Circle CenterX=5.8875 CenterY=78.339 CenterZ=0 NormalX=0 NormalY=0 NormalZ=1 AngleXU=0 Radius=2
  constraints (19):
    c: DistanceY(g-1,g0) = 78.339
    c: DistanceX(g-1,g0) = 5.8875
    c: Diameter(g0) = 4
    c: Coincident(g1,g2)
    c: Coincident(g2,g3)
    c: Coincident(g3,g4)
    c: Coincident(g4,g5)
    c: Coincident(g5,g6)
    c: Coincident(g6,g1)
    c: Equal(g1, g2-g6) x5
    c: PointOnObject(g1,g7)
    c: PointOnObject(g2,g7)
    c: PointOnObject(g3,g7)
    c: PointOnObject(g4,g7)
    c: PointOnObject(g5,g7)
    c: PointOnObject(g6,g7)
    c: Coincident(g7,g0)
    c: Horizontal(g1,g4)
    c: Equal(g7,g0)
FEATURE [PartDesign::Mirrored] Mirrored  label="TelescopingBarInsertArmMirror"
  BaseFeature = -> Pad007
  MirrorPlane = -> Sketch010 [V_Axis]
  Originals = -> [Pad007]
  Placement = pos=(0,0,0) rot=(1,0,0;1.5708rad)
FEATURE [PartDesign::Pocket] Pocket003  label="CrosspinHolePocket"
  BaseFeature = -> Mirrored
  Length = 5
  Length2 = 100
  Midplane = true
  Placement = pos=(0,0,0) rot=(1,0,0;1.5708rad)
  Profile = -> Sketch011
  Type = 1
FEATURE [PartDesign::Fillet] Fillet  label="ComfortFillet"
  Base = -> Pocket003 [Edge86]
  BaseFeature = -> Pocket003
  Placement = pos=(0,0,0) rot=(1,0,0;1.5708rad)
  Radius = 5
  SupportTransform = false
  expr: Radius = <<ProjectSettings>>.TelescopingPadComfortFilletRadius
FEATURE [Spreadsheet::Sheet] Spreadsheet004  label="CentralPadSettings"
  cells = A1=PadThickness; B1(PadThickness)==<<PadBodyPad>>.Length; A2=LockingButtonHoleDepth; B2(LockingButtonHoleDepth)==<<P90Measurements>>.PadWidestWidthOuterShoulderDistanceFromReferencePoint + <<TelescopingBarSettings>>.BarThickness + <<TelescopingBarSettings>>.LockingPinHeight * 3 + SpringMaxHeight; A3=SpringMaxHeight; B3(SpringMaxHeight)==20mm
FEATURE [Sketcher::SketchObject] Sketch014  label="CentralPadTelescopingBarInsertArmSketch"
  FullyConstrained = true
  MapMode = 5
  Placement = pos=(0,0,0) rot=(1,0,0;1.5708rad)
  Support = -> [XZ_Plane]
  expr: Constraints[34] = <<ProjectSettings>>.BarHeight / 3 + <<ProjectSettings>>.TightTolerance * 2
  expr: Constraints[16] = <<P90Measurements>>.PadThinnestWidth / 2
  expr: Constraints[13] = <<ProjectSettings>>.BarHeight + <<ProjectSettings>>.TightTolerance * 2
  expr: Constraints[10] = <<P90Measurements>>.PadWidestWidth / 2
  expr: Constraints[12] = <<P90Measurements>>.PadWidestWidthOuterShoulderDistanceFromReferencePoint
  expr: Constraints[11] = <<ProjectSettings>>.BarThickness + <<ProjectSettings>>.LooseTolerance * 2
  sketch-geometry (14):
    g0: LineSegment StartX=31.2159 StartY=70.739 StartZ=0 EndX=31.2159 EndY=75.739 EndZ=0
    g1: LineSegment StartX=31.2159 StartY=85.939 StartZ=0 EndX=25.6159 EndY=85.939 EndZ=0
    g2: LineSegment StartX=25.6159 StartY=85.939 StartZ=0 EndX=25.6159 EndY=70.739 EndZ=0
    g3: LineSegment StartX=25.6159 StartY=70.739 StartZ=0 EndX=31.2159 EndY=70.739 EndZ=0
    g4: LineSegment StartX=35.7859 StartY=70.739 StartZ=0 EndX=35.7859 EndY=75.739 EndZ=0
    g5: LineSegment StartX=22.5044 StartY=106.348 StartZ=0 EndX=22.5044 EndY=50.3301 EndZ=0
    g6: ArcOfCircle CenterX=31.2159 CenterY=85.939 CenterZ=0 NormalX=0 NormalY=0 NormalZ=1 AngleXU=0 Radius=4.57 StartAngle=2.3e-15 EndAngle=0.610865
    g7: ArcOfCircle CenterX=31.2159 CenterY=70.739 CenterZ=0 NormalX=0 NormalY=0 NormalZ=1 AngleXU=0 Radius=4.57 StartAngle=5.67232 EndAngle=6.28319
    g8: LineSegment StartX=22.5044 StartY=50.3301 StartZ=0 EndX=34.9594 EndY=68.1178 EndZ=0
    g9: LineSegment StartX=22.5044 StartY=106.348 StartZ=0 EndX=34.9594 EndY=88.5602 EndZ=0
    g10: LineSegment StartX=31.2159 StartY=80.939 StartZ=0 EndX=35.7859 EndY=80.939 EndZ=0
    g11: LineSegment StartX=31.2159 StartY=75.739 StartZ=0 EndX=35.7859 EndY=75.739 EndZ=0
    g12: LineSegment StartX=31.2159 StartY=80.939 StartZ=0 EndX=31.2159 EndY=85.939 EndZ=0
    g13: LineSegment StartX=35.7859 StartY=80.939 StartZ=0 EndX=35.7859 EndY=85.939 EndZ=0
  constraints (38):
    c: Vertical(g0)
    c: Coincident(g12,g1)
    c: Horizontal(g1)
    c: Coincident(g1,g2)
    c: Vertical(g2)
    c: Coincident(g2,g3)
    c: Coincident(g3,g0)
    c: Vertical(g5)
    c: Vertical(g4)
    c: Horizontal(g3)
    c: DistanceX(g-1,g2) = 25.6159
    c: DistanceX(g1,g1) = 5.6
    c: DistanceY(g-1,g2) = 70.739
    c: DistanceY(g0,g12) = 15.2
    c: Coincident(g6,g12)
    c: Coincident(g7,g0)
    c: DistanceX(g-1,g5) = 22.5044
    c: Coincident(g8,g5)
    c: Coincident(g9,g5)
    c: Tangent(g7,g4) = -1.5708
    c: Tangent(g9,g6) = 1.5708
    c: Tangent(g8,g7) = -1.5708
    c: Diameter(g6) = 9.14
    c: Equal(g8,g9)
    c: Angle(g4,g8) = 2.53073
    c: Horizontal(g11)
    c: Horizontal(g10)
    c: Coincident(g0,g11)
    c: Coincident(g12,g10)
    c: Tangent(g0,g12)
    c: Coincident(g4,g11)
    c: Coincident(g13,g10)
    c: Tangent(g4,g13)
    c: Tangent(g6,g13) = -1.5708
    c: DistanceY(g4,g10) = 5.2
    c: Equal(g12,g0)
    c: Angle(g5,g9) = 0.610865  'BarArmAngle'
    c: DistanceX(g10,g10) = 4.57  'BarArmWallThickness'
FEATURE [PartDesign::Pad] Pad008  label="CentralPadTelescopingBarInsertArmPad"
  BaseFeature = -> Pocket001
  Direction = (1,1,1)
  Length = 18
  Length2 = 100
  Placement = pos=(0,0,0) rot=(1,0,0;1.5708rad)
  Profile = -> Sketch014
  Reversed = true
  Type = 0
  expr: Length = <<CentralPadSettings>>.PadThickness
FEATURE [PartDesign::Mirrored] Mirrored001  label="CentralPadTelescopingBarInsertArmMirror"
  BaseFeature = -> Pad008
  MirrorPlane = -> Sketch014 [V_Axis]
  Originals = -> [Pad008]
  Placement = pos=(0,0,0) rot=(1,0,0;1.5708rad)
FEATURE [Sketcher::SketchObject] Sketch017  label="LockingPinBodySketch"
  FullyConstrained = true
  MapMode = 5
  Placement = pos=(0,0,0) rot=(0.57735,0.57735,0.57735;2.0944rad)
  Support = -> [YZ_Plane005]
  expr: Constraints[6] = <<ProjectSettings>>.LockingPinWidth
  expr: Constraints[9] = <<ProjectSettings>>.LockingPinHeight
  sketch-geometry (4):
    g0: LineSegment StartX=-2.38125 StartY=2.2 StartZ=0 EndX=2.38125 EndY=2.2 EndZ=0
    g1: LineSegment StartX=2.38125 StartY=2.2 StartZ=0 EndX=2.38125 EndY=-2.2 EndZ=0
    g2: LineSegment StartX=2.38125 StartY=-2.2 StartZ=0 EndX=-2.38125 EndY=-2.2 EndZ=0
    g3: LineSegment StartX=-2.38125 StartY=-2.2 StartZ=0 EndX=-2.38125 EndY=2.2 EndZ=0
  constraints (10):
    c: Coincident(g0,g1)
    c: Coincident(g1,g2)
    c: Coincident(g2,g3)
    c: Coincident(g3,g0)
    c: Horizontal(g2)
    c: Vertical(g1)
    c: DistanceX(g0,g0) = 4.7625
    c: Symmetric(g2,g0,g-1)
    c: Symmetric(g0,g0,g-2)
    c: DistanceY(g3,g3) = 4.4
FEATURE [PartDesign::Pad] Pad010  label="LockingPinBodyPad"
  Direction = (1,1,1)
  Length = 61.4468
  Length2 = 100
  Midplane = true
  Placement = pos=(0,0,0) rot=(0.57735,0.57735,0.57735;2.0944rad)
  Profile = -> Sketch017
  Type = 0
  expr: Length = Sketch010.Constraints.DistanceFromCenterlineToOutsideOfBarInsertArm * 2 - <<TelescopingBarSettings>>.BarThickness * 3 - <<ProjectSettings>>.LooseTolerance * 2
FEATURE [Sketcher::SketchObject] Sketch018  label="LockingPinHoleSketch"
  FullyConstrained = true
  MapMode = 5
  Placement = pos=(0,0,0) rot=(0.57735,0.57735,0.57735;2.0944rad)
  Support = -> [YZ_Plane]
  expr: Constraints[11] = <<P90Measurements>>.PadWidestWidthOuterShoulderDistanceFromReferencePoint + <<TelescopingBarSettings>>.BarHeight + <<TelescopingBarSettings>>.LockingPinHeight + <<ProjectSettings>>.LooseTolerance * 2
  expr: Constraints[10] = <<ProjectSettings>>.WallThickness
  expr: Constraints[9] = <<P90Measurements>>.PadWidestWidthOuterShoulderDistanceFromReferencePoint + (<<TelescopingBarSettings>>.BarHeight - <<TelescopingBarSettings>>.LockingPinHeight) / 2
  expr: Constraints[8] = <<ProjectSettings>>.LockingPinWidth + <<ProjectSettings>>.LooseTolerance * 2
  sketch-geometry (4):
    g0: LineSegment StartX=4 StartY=90.039 StartZ=0 EndX=9.3625 EndY=90.039 EndZ=0
    g1: LineSegment StartX=9.3625 StartY=90.039 StartZ=0 EndX=9.3625 EndY=74.089 EndZ=0
    g2: LineSegment StartX=9.3625 StartY=74.089 StartZ=0 EndX=4 EndY=74.089 EndZ=0
    g3: LineSegment StartX=4 StartY=74.089 StartZ=0 EndX=4 EndY=90.039 EndZ=0
  constraints (12):
    c: Coincident(g0,g1)
    c: Coincident(g1,g2)
    c: Coincident(g2,g3)
    c: Coincident(g3,g0)
    c: Horizontal(g0)
    c: Horizontal(g2)
    c: Vertical(g1)
    c: Vertical(g3)
    c: DistanceX(g0,g0) = 5.3625
    c: DistanceY(g-1,g2) = 74.089
    c: DistanceX(g-1,g2) = 4
    c: DistanceY(g-1,g0) = 90.039
FEATURE [PartDesign::Pocket] Pocket007  label="LockingPinHolePocket"
  BaseFeature = -> Mirrored001
  Length = 62.0468
  Length2 = 100
  Midplane = true
  Placement = pos=(0,0,0) rot=(1,0,0;1.5708rad)
  Profile = -> Sketch018
  Type = 0
  expr: Length = <<LockingPinBodyPad>>.Length + <<ProjectSettings>>.LooseTolerance * 2
FEATURE [Sketcher::SketchObject] Sketch019  label="LockingButtonHoleSketch"
  FullyConstrained = true
  MapMode = 5
  Support = -> [XY_Plane]
  expr: Constraints[14] = <<ProjectSettings>>.StandardFillet
  expr: Constraints[17] = <<ProjectSettings>>.LockingButtonWidth + <<ProjectSettings>>.LooseTolerance * 2
  expr: Constraints[16] = <<ProjectSettings>>.LockingButtonHeight + <<ProjectSettings>>.LooseTolerance * 2
  expr: Constraints[18] = <<ProjectSettings>>.WallThickness
  sketch-geometry (8):
    g0: LineSegment StartX=-3.3 StartY=14.6 StartZ=0 EndX=3.3 EndY=14.6 EndZ=0
    g1: LineSegment StartX=5.3 StartY=12.6 StartZ=0 EndX=5.3 EndY=6 EndZ=0
    g2: LineSegment StartX=3.3 StartY=4 StartZ=0 EndX=-3.3 EndY=4 EndZ=0
    g3: LineSegment StartX=-5.3 StartY=6 StartZ=0 EndX=-5.3 EndY=12.6 EndZ=0
    g4: ArcOfCircle CenterX=-3.3 CenterY=12.6 CenterZ=0 NormalX=0 NormalY=0 NormalZ=1 AngleXU=0 Radius=2 StartAngle=1.5708 EndAngle=3.14159
    g5: ArcOfCircle CenterX=3.3 CenterY=12.6 CenterZ=0 NormalX=0 NormalY=0 NormalZ=1 AngleXU=0 Radius=2 StartAngle=0 EndAngle=1.5708
    g6: ArcOfCircle CenterX=3.3 CenterY=6 CenterZ=0 NormalX=0 NormalY=0 NormalZ=1 AngleXU=0 Radius=2 StartAngle=4.71239 EndAngle=6.28319
    g7: ArcOfCircle CenterX=-3.3 CenterY=6 CenterZ=0 NormalX=0 NormalY=0 NormalZ=1 AngleXU=0 Radius=2 StartAngle=3.14159 EndAngle=4.71239
  constraints (19):
    c: Horizontal(g2)
    c: Vertical(g1)
    c: Vertical(g3)
    c: Tangent(g3,g4) = 1.5708
    c: Tangent(g0,g4) = 1.5708
    c: Tangent(g0,g5) = 1.5708
    c: Tangent(g1,g5) = 1.5708
    c: Tangent(g2,g6) = 1.5708
    c: Tangent(g1,g6) = 1.5708
    c: Tangent(g2,g7) = 1.5708
    c: Tangent(g3,g7) = 1.5708
    c: Equal(g7,g4)
    c: Equal(g4,g5)
    c: Equal(g5,g6)
    c: Radius(g5) = 2
    c: Symmetric(g0,g0,g-2)
    c: DistanceY(g2,g0) = 10.6
    c: DistanceX(g3,g1) = 10.6
    c: DistanceY(g-1,g2) = 4
FEATURE [PartDesign::Pocket] Pocket008  label="LockingButtonHolePocket"
  BaseFeature = -> Pocket007
  Length = 111.914
  Length2 = 100
  Placement = pos=(0,0,0) rot=(1,0,0;1.5708rad)
  Profile = -> Sketch019
  Reversed = true
  Type = 0
  expr: Length = <<CentralPadSettings>>.LockingButtonHoleDepth
FEATURE [Sketcher::SketchObject] Sketch020  label="ButtonBodySketch"
  AttachmentOffset = pos=(0,0,2) rot=(0,0,1;0rad)
  FullyConstrained = true
  MapMode = 5
  Placement = pos=(0,0,2) rot=(0,0,1;0rad)
  Support = -> [XY_Plane006]
  expr: Constraints[17] = <<ProjectSettings>>.LockingButtonWidth - <<ProjectSettings>>.LooseTolerance * 2
  expr: Constraints[16] = <<ProjectSettings>>.LockingButtonWidth - <<ProjectSettings>>.LooseTolerance * 2
  expr: Constraints[10] = <<ProjectSettings>>.StandardFillet
  sketch-geometry (8):
    g0: LineSegment StartX=-2.7 StartY=4.7 StartZ=0 EndX=2.7 EndY=4.7 EndZ=0
    g1: LineSegment StartX=4.7 StartY=2.7 StartZ=0 EndX=4.7 EndY=-2.7 EndZ=0
    g2: LineSegment StartX=2.7 StartY=-4.7 StartZ=0 EndX=-2.7 EndY=-4.7 EndZ=0
    g3: LineSegment StartX=-4.7 StartY=-2.7 StartZ=0 EndX=-4.7 EndY=2.7 EndZ=0
    g4: ArcOfCircle CenterX=-2.7 CenterY=2.7 CenterZ=0 NormalX=0 NormalY=0 NormalZ=1 AngleXU=0 Radius=2 StartAngle=1.5708 EndAngle=3.14159
    g5: ArcOfCircle CenterX=2.7 CenterY=2.7 CenterZ=0 NormalX=0 NormalY=0 NormalZ=1 AngleXU=0 Radius=2 StartAngle=0 EndAngle=1.5708
    g6: ArcOfCircle CenterX=2.7 CenterY=-2.7 CenterZ=0 NormalX=0 NormalY=0 NormalZ=1 AngleXU=0 Radius=2 StartAngle=4.71239 EndAngle=6.28319
    g7: ArcOfCircle CenterX=-2.7 CenterY=-2.7 CenterZ=0 NormalX=0 NormalY=0 NormalZ=1 AngleXU=0 Radius=2 StartAngle=3.14159 EndAngle=4.71239
  constraints (18):
    c: Horizontal(g0)
    c: Vertical(g1)
    c: Tangent(g3,g4) = 1.5708
    c: Tangent(g0,g4) = 1.5708
    c: Tangent(g1,g5) = 1.5708
    c: Tangent(g0,g5) = 1.5708
    c: Tangent(g1,g6) = 1.5708
    c: Tangent(g2,g6) = 1.5708
    c: Tangent(g2,g7) = 1.5708
    c: Tangent(g3,g7) = 1.5708
    c: Radius(g4) = 2
    c: Equal(g4,g5)
    c: Equal(g4,g6)
    c: Equal(g4,g7)
    c: Symmetric(g2,g2,g-2)
    c: Symmetric(g3,g3,g-1)
    c: DistanceX(g3,g1) = 9.4
    c: DistanceY(g2,g0) = 9.4
FEATURE [PartDesign::Pad] Pad011  label="ButtonBodyPad"
  Direction = (1,1,1)
  Length = 88.939
  Length2 = 10
  Profile = -> Sketch020
  Type = 4
  expr: Length = <<ProjectSettings>>.LockingButtonHoleDepth - <<ProjectSettings>>.SpringMaxHeight
  expr: Length2 = <<ProjectSettings>>.LockingButtonActuationDistance + 4mm
FEATURE [Sketcher::SketchObject] Sketch021  label="ButtonLockingPinHoleSketch"
  FullyConstrained = true
  MapMode = 5
  Placement = pos=(0,0,0) rot=(0.57735,0.57735,0.57735;2.0944rad)
  Support = -> [YZ_Plane006]
  expr: Constraints[8] = <<P90Measurements>>.PadWidestWidthOuterShoulderDistanceFromReferencePoint + <<ProjectSettings>>.BarHeight / 2
  expr: Constraints[7] = <<ProjectSettings>>.LockingPinWidth + <<ProjectSettings>>.TightTolerance * 2
  expr: Constraints[9] = (<<ProjectSettings>>.LockingButtonWidth - <<ProjectSettings>>.LooseTolerance * 2) / 2
  expr: Constraints[11] = <<ProjectSettings>>.LockingPinHeight + <<ProjectSettings>>.TightTolerance * 2
  sketch-geometry (4):
    g0: LineSegment StartX=-4.7 StartY=82.839 StartZ=0 EndX=0.2625 EndY=82.839 EndZ=0
    g1: LineSegment StartX=0.2625 StartY=82.839 StartZ=0 EndX=0.2625 EndY=78.239 EndZ=0
    g2: LineSegment StartX=0.2625 StartY=78.239 StartZ=0 EndX=-4.7 EndY=78.239 EndZ=0
    g3: LineSegment StartX=-4.7 StartY=78.239 StartZ=0 EndX=-4.7 EndY=82.839 EndZ=0
  constraints (12):
    c: Coincident(g0,g1)
    c: Coincident(g1,g2)
    c: Coincident(g2,g3)
    c: Coincident(g3,g0)
    c: Horizontal(g2)
    c: Vertical(g1)
    c: Vertical(g3)
    c: DistanceX(g0,g0) = 4.9625
    c: DistanceY(g-1,g2) = 78.239
    c: DistanceX(g2,g-1) = 4.7
    c: Horizontal(g0)
    c: DistanceY(g3,g3) = 4.6
FEATURE [PartDesign::Pocket] Pocket009  label="ButtonLockingPinHolePocket"
  BaseFeature = -> Pad011
  Length = 5
  Length2 = 100
  Midplane = true
  Profile = -> Sketch021
  Type = 1
FEATURE [Sketcher::SketchObject] Sketch022  label="BCGHoleSketch"
  AttachmentOffset = pos=(0,0,5.2) rot=(0,0,1;0rad)
  FullyConstrained = true
  MapMode = 5
  Placement = pos=(0,-5.2,-1.2e-15) rot=(1,0,0;1.5708rad)
  Support = -> [XZ_Plane]
  expr: .AttachmentOffset.Base.z = <<DovetailBodyPad>>.Length
  expr: Constraints[2] = <<P90Measurements>>.PadBCGHoleDiameter + <<ProjectSettings>>.LooseTolerance * 2
  expr: Constraints[1] = <<P90Measurements>>.PadBCGHoleFromReferencePoint + <<P90Measurements>>.PadBCGHoleDiameter / 2
  sketch-geometry (1):
    g0: Circle CenterX=0 CenterY=79.6417 CenterZ=0 NormalX=0 NormalY=0 NormalZ=1 AngleXU=0 Radius=3.8179
  constraints (3):
    c: PointOnObject(g0,g-2)
    c: DistanceY(g-1,g0) = 79.6417
    c: Diameter(g0) = 7.6358
FEATURE [PartDesign::Pocket] Pocket010  label="BCGHolePocket"
  BaseFeature = -> Pocket008
  Length = 9.2
  Length2 = 100
  Placement = pos=(0,0,0) rot=(1,0,0;1.5708rad)
  Profile = -> Sketch022
  Refine = true
  Type = 0
  expr: Length = <<DovetailBodyPad>>.Length + <<ProjectSettings>>.WallThickness
FEATURE [Sketcher::SketchObject] Sketch024  label="BarCrosspinHoleSketch001"
  FullyConstrained = true
  MapMode = 5
  Placement = pos=(0,0,0) rot=(0.57735,0.57735,0.57735;2.0944rad)
  Support = -> [YZ_Plane007]
  expr: Constraints[1] = <<ProjectSettings>>.CrosspinWidth
  expr: Constraints[2] = <<ProjectSettings>>.WallThickness + <<ProjectSettings>>.CrosspinWidth / 2 + <<ProjectSettings>>.TightTolerance
  sketch-geometry (8):
    g0: Circle CenterX=-6.1 CenterY=0 CenterZ=0 NormalX=0 NormalY=0 NormalZ=1 AngleXU=0 Radius=2
    g1: LineSegment StartX=-4.1 StartY=-2.6457e-12 StartZ=0 EndX=-5.1 EndY=1.73205 EndZ=0
    g2: LineSegment StartX=-5.1 StartY=1.73205 StartZ=0 EndX=-7.1 EndY=1.73205 EndZ=0
    g3: LineSegment StartX=-7.1 StartY=1.73205 StartZ=0 EndX=-8.1 EndY=-2.6457e-12 EndZ=0
    g4: LineSegment StartX=-8.1 StartY=-2.6457e-12 StartZ=0 EndX=-7.1 EndY=-1.73205 EndZ=0
    g5: LineSegment StartX=-7.1 StartY=-1.73205 StartZ=0 EndX=-5.1 EndY=-1.73205 EndZ=0
    g6: LineSegment StartX=-5.1 StartY=-1.73205 StartZ=0 EndX=-4.1 EndY=-2.6457e-12 EndZ=0
    g7: Circle CenterX=-6.1 CenterY=0 CenterZ=0 NormalX=0 NormalY=0 NormalZ=1 AngleXU=0 Radius=2
  constraints (19):
    c: PointOnObject(g0,g-1)
    c: Diameter(g0) = 4
    c: DistanceX(g0,g-1) = 6.1
    c: Coincident(g1,g2)
    c: Coincident(g2,g3)
    c: Coincident(g3,g4)
    c: Coincident(g4,g5)
    c: Coincident(g5,g6)
    c: Coincident(g6,g1)
    c: Equal(g1, g2-g6) x5
    c: PointOnObject(g1,g7)
    c: PointOnObject(g2,g7)
    c: PointOnObject(g3,g7)
    c: PointOnObject(g4,g7)
    c: PointOnObject(g5,g7)
    c: PointOnObject(g6,g7)
    c: Coincident(g7,g0)
    c: PointOnObject(g6,g0)
    c: Horizontal(g1,g3)
FEATURE [Sketcher::SketchObject] Sketch025  label="MainBarSketch001"
  FullyConstrained = true
  MapMode = 5
  Placement = pos=(0,0,0) rot=(1,0,0;1.5708rad)
  Support = -> [XZ_Plane007]
  expr: Constraints[8] = <<ProjectSettings>>.BarThickness
  expr: Constraints[9] = <<ProjectSettings>>.BarHeight
  sketch-geometry (4):
    g0: LineSegment StartX=-2.5 StartY=7.5 StartZ=0 EndX=2.5 EndY=7.5 EndZ=0
    g1: LineSegment StartX=2.5 StartY=7.5 StartZ=0 EndX=2.5 EndY=-7.5 EndZ=0
    g2: LineSegment StartX=2.5 StartY=-7.5 StartZ=0 EndX=-2.5 EndY=-7.5 EndZ=0
    g3: LineSegment StartX=-2.5 StartY=-7.5 StartZ=0 EndX=-2.5 EndY=7.5 EndZ=0
  constraints (10):
    c: Coincident(g0,g1)
    c: Coincident(g1,g2)
    c: Coincident(g2,g3)
    c: Coincident(g3,g0)
    c: Horizontal(g2)
    c: Vertical(g3)
    c: Symmetric(g1,g0,g-1)
    c: Symmetric(g0,g0,g-2)
    c: DistanceX(g0,g0) = 5
    c: DistanceY(g3,g3) = 15
FEATURE [PartDesign::Pad] Pad013  label="MainBarPad001"
  Direction = (1,1,1)
  Length = 265
  Length2 = 100
  Placement = pos=(0,0,0) rot=(1,0,0;1.5708rad)
  Profile = -> Sketch025
  Type = 0
  expr: Length = <<ProjectSettings>>.BarLength
FEATURE [PartDesign::Pocket] Pocket011  label="BarCrosspinHolePocket001"
  BaseFeature = -> Pad013
  Length = 5
  Length2 = 100
  Midplane = true
  Placement = pos=(0,0,0) rot=(1,0,0;1.5708rad)
  Profile = -> Sketch024
  Type = 1
FEATURE [Sketcher::SketchObject] Sketch027  label="BarRackSketch001"
  FullyConstrained = true
  MapMode = 5
  Placement = pos=(0,0,0) rot=(0.57735,0.57735,0.57735;2.0944rad)
  Support = -> [YZ_Plane007]
  expr: Constraints[2] = <<ProjectSettings>>.LockingPinWidth + <<ProjectSettings>>.TightTolerance * 2
  expr: Constraints[4] = <<ProjectSettings>>.BarHeight / 3
  expr: Constraints[3] = <<ProjectSettings>>.BarHeight / 2
  expr: Constraints[8] = <<ProjectSettings>>.BarRackFillet
  expr: Constraints[13] = <<ProjectSettings>>.BarRackFillet
  expr: Constraints[14] = <<ProjectSettings>>.BarRackStartOffset
  expr: Constraints[18] = <<ProjectSettings>>.BarRackLength
  sketch-geometry (7):
    g0: LineSegment StartX=-35.1371 StartY=-7.5 StartZ=0 EndX=-19 EndY=-7.5 EndZ=0
    g1: LineSegment StartX=-21 StartY=-2.5 StartZ=0 EndX=-25.9625 EndY=-2.5 EndZ=0
    g2: ArcOfCircle CenterX=-35.1371 CenterY=-5.5 CenterZ=0 NormalX=0 NormalY=0 NormalZ=1 AngleXU=0 Radius=2 StartAngle=4.71239 EndAngle=5.23713
    g3: LineSegment StartX=-34.1352 StartY=-7.23091 StartZ=0 EndX=-25.9625 EndY=-2.5 EndZ=0
    g4: LineSegment StartX=-21 StartY=-2.5 StartZ=0 EndX=-21 EndY=-5.5 EndZ=0
    g5: ArcOfCircle CenterX=-19 CenterY=-5.5 CenterZ=0 NormalX=0 NormalY=0 NormalZ=1 AngleXU=0 Radius=2 StartAngle=3.14159 EndAngle=4.71239
    g6: LineSegment StartX=-34.1352 StartY=-7.23091 StartZ=0 EndX=-34.6 EndY=-7.5 EndZ=0
  constraints (19):
    c: Horizontal(g0)
    c: Horizontal(g1)
    c: DistanceX(g1,g1) = 4.9625
    c: DistanceY(g0,g-1) = 7.5
    c: DistanceY(g0,g1) = 5
    c: Tangent(g0,g2) = -1.5708
    c: Coincident(g3,g1)
    c: Tangent(g3,g2) = -1.5708
    c: Radius(g2) = 2
    c: Coincident(g4,g1)
    c: Vertical(g4)
    c: Tangent(g5,g4) = -1.5708
    c: Tangent(g0,g5) = -1.5708
    c: Radius(g5) = 2
    c: DistanceX(g1,g-1) = 21
    c: Coincident(g6,g2)
    c: PointOnObject(g6,g0)
    c: Tangent(g6,g2)
    c: DistanceX(g6,g4) = 13.6
FEATURE [PartDesign::Pocket] Pocket013  label="BarRackPocket001"
  BaseFeature = -> Pocket011
  Length = 5
  Length2 = 100
  Midplane = true
  Placement = pos=(0,0,0) rot=(1,0,0;1.5708rad)
  Profile = -> Sketch027
  Type = 1
FEATURE [Sketcher::SketchObject] Sketch028  label="FinalSlotSketch001"
  FullyConstrained = true
  MapMode = 5
  Placement = pos=(0,0,0) rot=(0.57735,0.57735,0.57735;2.0944rad)
  Support = -> [YZ_Plane007]
  expr: Constraints[5] = <<ProjectSettings>>.BarLength - <<ProjectSettings>>.BarThickness - <<ProjectSettings>>.WallThickness
  expr: Constraints[2] = <<ProjectSettings>>.LockingPinWidth + <<ProjectSettings>>.LooseTolerance * 2
  expr: Constraints[4] = <<ProjectSettings>>.BarHeight / 3
  expr: Constraints[3] = -1 * <<ProjectSettings>>.BarHeight / 2
  expr: Constraints[14] = <<ProjectSettings>>.BarRackFillet
  sketch-geometry (6):
    g0: LineSegment StartX=-248.637 StartY=-7.5 StartZ=0 EndX=-258 EndY=-7.5 EndZ=0
    g1: LineSegment StartX=-256 StartY=-2.5 StartZ=0 EndX=-250.637 EndY=-2.5 EndZ=0
    g2: ArcOfCircle CenterX=-258 CenterY=-5.5 CenterZ=0 NormalX=0 NormalY=0 NormalZ=1 AngleXU=0 Radius=2 StartAngle=4.71239 EndAngle=6.28319
    g3: ArcOfCircle CenterX=-248.637 CenterY=-5.5 CenterZ=0 NormalX=0 NormalY=0 NormalZ=1 AngleXU=0 Radius=2 StartAngle=3.14159 EndAngle=4.71239
    g4: LineSegment StartX=-250.637 StartY=-2.5 StartZ=0 EndX=-250.637 EndY=-5.5 EndZ=0
    g5: LineSegment StartX=-256 StartY=-2.5 StartZ=0 EndX=-256 EndY=-5.5 EndZ=0
  constraints (16):
    c: Horizontal(g0)
    c: Horizontal(g1)
    c: DistanceX(g1,g1) = 5.3625
    c: DistanceY(g-1,g0) = -7.5
    c: DistanceY(g0,g1) = 5
    c: DistanceX(g1,g-1) = 256
    c: Coincident(g4,g1)
    c: Vertical(g4)
    c: Coincident(g5,g1)
    c: Vertical(g5)
    c: Tangent(g2,g5) = 1.5708
    c: Tangent(g3,g4) = -1.5708
    c: Tangent(g0,g3) = 1.5708
    c: Tangent(g0,g2) = 1.5708
    c: Radius(g3) = 2
    c: Equal(g3,g2)
FEATURE [PartDesign::LinearPattern] LinearPattern001  label="BarRackPattern001"
  BaseFeature = -> Pocket013
  Direction = -> Sketch027 [H_Axis]
  Length = 207.4
  Occurrences = 6
  Originals = -> [Pocket013]
  Placement = pos=(0,0,0) rot=(1,0,0;1.5708rad)
  Reversed = true
  expr: Length = <<ProjectSettings>>.BarLength - <<ProjectSettings>>.BarRackStartOffset - <<CentralPadTelescopingBarInsertArmPad>>.Length - <<ProjectSettings>>.BarEndcapThickness - <<ProjectSettings>>.BarRackLength
  expr: Occurrences = floor(Length / (<<ProjectSettings>>.BarRackLength + <<CentralPadTelescopingBarInsertArmPad>>.Length))
FEATURE [PartDesign::Pocket] Pocket012  label="FinalSlotPad001"
  BaseFeature = -> LinearPattern001
  Length = 5
  Length2 = 100
  Midplane = true
  Placement = pos=(0,0,0) rot=(1,0,0;1.5708rad)
  Profile = -> Sketch028
  Refine = true
  Type = 1
FEATURE [PartDesign::Fillet] Fillet004  label="Slide Fillet"
  Base = -> Pad010 [Edge8]
  BaseFeature = -> Pad010
  Placement = pos=(0,0,0) rot=(0.57735,0.57735,0.57735;2.0944rad)
  Radius = 2
  SupportTransform = false
FEATURE [Sketcher::SketchObject] Sketch029  label="LightningCutSketch"
  FullyConstrained = true
  MapMode = 5
  Placement = pos=(0,0,0) rot=(1,0,0;1.5708rad)
  Support = -> [XZ_Plane002]
  expr: Constraints[11] = <<ProjectSettings>>.WallThickness * 2
  expr: Constraints[5] = <<P90Measurements>>.ButtOverallHeight - <<ProjectSettings>>.WallThickness * 2
  expr: Constraints[2] = <<P90Measurements>>.PadWidestWidth - <<ProjectSettings>>.TelescopingPadComfortFilletRadius * 3
  sketch-geometry (6):
    g0: ArcOfCircle CenterX=-1.1391e-12 CenterY=26.1159 CenterZ=0 NormalX=0 NormalY=0 NormalZ=1 AngleXU=0 Radius=18.1159 StartAngle=3.14159 EndAngle=4.71239
    g1: LineSegment StartX=18.1159 StartY=26.1159 StartZ=0 EndX=18.1159 EndY=94.1023 EndZ=0
    g2: LineSegment StartX=-18.1159 StartY=26.1159 StartZ=0 EndX=-18.1159 EndY=94.1023 EndZ=0
    g3: ArcOfCircle CenterX=-6.2e-15 CenterY=94.1023 CenterZ=0 NormalX=0 NormalY=0 NormalZ=1 AngleXU=0 Radius=18.1159 StartAngle=1.5708 EndAngle=3.14159
    g4: ArcOfCircle CenterX=-6.2e-15 CenterY=94.1023 CenterZ=0 NormalX=0 NormalY=0 NormalZ=1 AngleXU=0 Radius=18.1159 StartAngle=0 EndAngle=1.5708
    g5: ArcOfCircle CenterX=2.401e-13 CenterY=26.1159 CenterZ=0 NormalX=0 NormalY=0 NormalZ=1 AngleXU=0 Radius=18.1159 StartAngle=4.71239 EndAngle=6.28319
  constraints (15):
    c: Vertical(g2)
    c: Vertical(g1)
    c: DistanceX(g2,g1) = 36.2318
    c: Tangent(g2,g3) = 1.5708
    c: Tangent(g1,g4) = -1.5708
    c: DistanceY(g-1,g3) = 112.218
    c: Tangent(g4,g3) = -1.5708
    c: PointOnObject(g3,g-2)
    c: Symmetric(g2,g1,g-2)
    c: Tangent(g1,g5) = -1.5708
    c: Tangent(g0,g2) = 1.5708
    c: DistanceY(g-1,g5) = 8
    c: Tangent(g0,g5) = -1.5708
    c: PointOnObject(g0,g-2)
    c: Horizontal(g0,g1)
FEATURE [PartDesign::Pocket] Pocket014  label="LightningCutPocket"
  BaseFeature = -> Fillet
  Length = 12
  Length2 = 100
  Placement = pos=(0,0,0) rot=(1,0,0;1.5708rad)
  Profile = -> Sketch029
  Type = 0
  expr: Length = <<ProjectSettings>>.TelescopingBarInsertDepth
FEATURE [PartDesign::Fillet] Fillet016  label="BarHoleLargeFillet"
  Base = -> Pocket010 [Edge203,Edge186,Edge187,Edge204,Edge49,Edge75,Edge48,Edge74,Edge217,Edge123]
  BaseFeature = -> Pocket010
  Placement = pos=(0,0,0) rot=(1,0,0;1.5708rad)
  Radius = 2
  SupportTransform = false
FEATURE [PartDesign::Fillet] Fillet017  label="LockingBodytHardEdgeFillet"
  Base = -> Fillet016 [Edge1,Edge68,Edge133,Edge164]
  BaseFeature = -> Fillet016
  Placement = pos=(0,0,0) rot=(1,0,0;1.5708rad)
  Radius = 2
  SupportTransform = false
FEATURE [PartDesign::Fillet] Fillet018
  Base = -> Pocket009 [Face2]
  BaseFeature = -> Pocket009
  Radius = 2
  SupportTransform = false
FEATURE [PartDesign::Body] Body005  label="LockingButton"
  Group = -> [Sketch020,Pad011,Sketch021,Pocket009,Fillet018]
  Origin = -> Origin006
  Placement = pos=(0,9.3,0) rot=(0,0,1;0rad)
  Tip = -> Fillet018
  expr: .Placement.Base.y = <<ProjectSettings>>.LockingButtonHeight / 2 + <<ProjectSettings>>.WallThickness + <<ProjectSettings>>.LooseTolerance
FEATURE [Sketcher::SketchObject] Sketch040  label="HorizontalScallopSketch"
  FullyConstrained = true
  MapMode = 5
  Placement = pos=(0,0,0) rot=(0.57735,0.57735,0.57735;2.0944rad)
  Support = -> [YZ_Plane002]
  expr: Constraints[2] = <<TelescoptingPadBodyPad>>.Length
  expr: Constraints[1] = <<ProjectSettings>>.ScallopRadius
  sketch-geometry (5):
    g0: Circle CenterX=21 CenterY=0 CenterZ=0 NormalX=0 NormalY=0 NormalZ=1 AngleXU=0 Radius=1.5
    g1: LineSegment StartX=21 StartY=1.5 StartZ=0 EndX=19.5 EndY=0 EndZ=0
    g2: LineSegment StartX=19.5 StartY=0 StartZ=0 EndX=21 EndY=-1.5 EndZ=0
    g3: LineSegment StartX=21 StartY=-1.5 StartZ=0 EndX=22.5 EndY=0 EndZ=0
    g4: LineSegment StartX=22.5 StartY=0 StartZ=0 EndX=21 EndY=1.5 EndZ=0
  constraints (15):
    c: PointOnObject(g0,g-1)
    c: Radius(g0) = 1.5
    c: DistanceX(g-1,g0) = 21
    c: PointOnObject(g1,g0)
    c: PointOnObject(g1,g0)
    c: Coincident(g1,g2)
    c: PointOnObject(g2,g0)
    c: PointOnObject(g1,g-1)
    c: Coincident(g2,g3)
    c: PointOnObject(g3,g0)
    c: Coincident(g3,g4)
    c: Coincident(g4,g1)
    c: Vertical(g1,g0)
    c: Vertical(g0,g2)
    c: PointOnObject(g3,g-1)
FEATURE [PartDesign::Pocket] Pocket022  label="HorizontalScallopPocket"
  BaseFeature = -> Pocket014
  Length = 5
  Length2 = 100
  Midplane = true
  Placement = pos=(0,0,0) rot=(1,0,0;1.5708rad)
  Profile = -> Sketch040
  Type = 1
FEATURE [PartDesign::LinearPattern] LinearPattern  label="HorizontalScallopLinearPattern"
  BaseFeature = -> Pocket022
  Direction = -> Z_Axis002
  Length = 120.218
  Occurrences = 36
  Originals = -> [Pocket022]
  Placement = pos=(0,0,0) rot=(1,0,0;1.5708rad)
  expr: Length = <<P90Measurements>>.ButtOverallHeight
  expr: Occurrences = floor(Length / (<<ProjectSettings>>.ScallopRadius * 2 + <<ProjectSettings>>.DistanceBetweenScallops))
FEATURE [Sketcher::SketchObject] Sketch041  label="VerticalScallopSketch"
  FullyConstrained = true
  MapMode = 5
  Support = -> [XY_Plane002]
  expr: Constraints[2] = <<P90Measurements>>.PadWidestWidth / 2 - <<ComfortFillet>>.Radius
  expr: Constraints[1] = <<TelescoptingPadBodyPad>>.Length
  expr: Constraints[0] = <<ProjectSettings>>.ScallopRadius
  sketch-geometry (5):
    g0: Circle CenterX=-20.6159 CenterY=21 CenterZ=0 NormalX=0 NormalY=0 NormalZ=1 AngleXU=0 Radius=1.5
    g1: LineSegment StartX=-22.1159 StartY=21 StartZ=0 EndX=-20.6159 EndY=22.5 EndZ=0
    g2: LineSegment StartX=-20.6159 StartY=22.5 StartZ=0 EndX=-19.1159 EndY=21 EndZ=0
    g3: LineSegment StartX=-19.1159 StartY=21 StartZ=0 EndX=-20.6159 EndY=19.5 EndZ=0
    g4: LineSegment StartX=-20.6159 StartY=19.5 StartZ=0 EndX=-22.1159 EndY=21 EndZ=0
  constraints (15):
    c: Radius(g0) = 1.5
    c: DistanceY(g-1,g0) = 21
    c: DistanceX(g0,g-1) = 20.6159
    c: PointOnObject(g1,g0)
    c: PointOnObject(g1,g0)
    c: Coincident(g1,g2)
    c: PointOnObject(g2,g0)
    c: Coincident(g2,g3)
    c: PointOnObject(g3,g0)
    c: Coincident(g3,g4)
    c: Coincident(g4,g1)
    c: Vertical(g1,g0)
    c: Vertical(g3,g0)
    c: Horizontal(g1,g0)
    c: Horizontal(g2,g0)
FEATURE [PartDesign::Pocket] Pocket023  label="VerticalScallopPocket"
  BaseFeature = -> LinearPattern
  Length = 5
  Length2 = 100
  Midplane = true
  Placement = pos=(0,0,0) rot=(1,0,0;1.5708rad)
  Profile = -> Sketch041
  Type = 1
FEATURE [PartDesign::LinearPattern] LinearPattern002  label="VerticalScallopLinearPattern"
  BaseFeature = -> Pocket023
  Direction = -> X_Axis002
  Length = 41.2318
  Occurrences = 12
  Originals = -> [Pocket023]
  Placement = pos=(0,0,0) rot=(1,0,0;1.5708rad)
  Refine = true
  expr: Length = <<P90Measurements>>.PadWidestWidth - <<ComfortFillet>>.Radius * 2
  expr: Occurrences = floor(Length / (<<ProjectSettings>>.ScallopRadius * 2 + <<ProjectSettings>>.DistanceBetweenScallops))
FEATURE [PartDesign::Fillet] Fillet023  label="BarArmFillet"
  Base = -> LinearPattern002 [Edge253,Edge659,Edge311,Edge685]
  BaseFeature = -> LinearPattern002
  Placement = pos=(0,0,0) rot=(1,0,0;1.5708rad)
  Radius = 2
  SupportTransform = false
  expr: Radius = <<ProjectSettings>>.StandardFillet
FEATURE [Sketcher::SketchObject] Sketch042  label="PaperworkLidNubSketch"
  AttachmentOffset = pos=(0,0,60.1091) rot=(0,0,1;0rad)
  FullyConstrained = true
  MapMode = 5
  Placement = pos=(0,0,60.1091) rot=(0,0,1;0rad)
  Support = -> [XY_Plane002]
  expr: Constraints[5] = <<ProjectSettings>>.PaperworkLidNubWidth + <<ProjectSettings>>.TightTolerance * 2
  expr: Constraints[6] = <<ProjectSettings>>.PaperworkLidNubHeight + <<ProjectSettings>>.TightTolerance * 2
  expr: Constraints[7] = <<LightningCutPocket>>.Length
  expr: .AttachmentOffset.Base.z = <<P90Measurements>>.ButtOverallHeight / 2
  expr: Constraints[8] = (<<P90Measurements>>.PadWidestWidth - <<ProjectSettings>>.TelescopingPadComfortFilletRadius * 3) / 2
  sketch-geometry (3):
    g0: LineSegment StartX=-18.1159 StartY=9.8 StartZ=0 EndX=-19.8159 EndY=10.9 EndZ=0
    g1: LineSegment StartX=-19.8159 StartY=10.9 StartZ=0 EndX=-18.1159 EndY=12 EndZ=0
    g2: LineSegment StartX=-18.1159 StartY=12 StartZ=0 EndX=-18.1159 EndY=9.8 EndZ=0
  constraints (9):
    c: Coincident(g0,g1)
    c: Coincident(g1,g2)
    c: Vertical(g2)
    c: Coincident(g2,g0)
    c: Equal(g1,g0)
    c: DistanceY(g2,g2) = 2.2
    c: DistanceX(g0,g0) = 1.7
    c: DistanceY(g-1,g1) = 12
    c: DistanceX(g1,g-1) = 18.1159
FEATURE [PartDesign::SubtractivePipe] SubtractivePipe  label="PaperworkLidNubSubtractivePipe"
  AuxilleryCurvelinear = true
  AuxillerySpineTangent = false
  BaseFeature = -> Fillet023
  Binormal = (0,0,0)
  Mode = 0
  Placement = pos=(0,0,0) rot=(1,0,0;1.5708rad)
  Profile = -> Sketch042
  Spine = -> Fillet023 [Edge501]
  SpineTangent = false
  Transformation = 0
  Transition = 0
FEATURE [PartDesign::Mirrored] Mirrored002  label="PaperworkLidNubSketchMirror"
  BaseFeature = -> SubtractivePipe
  MirrorPlane = -> Sketch042 [V_Axis]
  Originals = -> [SubtractivePipe]
  Placement = pos=(0,0,0) rot=(1,0,0;1.5708rad)
FEATURE [Sketcher::SketchObject] Sketch043  label="PaperworkLidMainSketch"
  FullyConstrained = true
  MapMode = 5
  Placement = pos=(0,0,0) rot=(1,0,0;1.5708rad)
  Support = -> [XZ_Plane011]
  expr: Constraints[2] = <<P90Measurements>>.PadWidestWidth - <<ProjectSettings>>.TelescopingPadComfortFilletRadius * 3 - <<ProjectSettings>>.LooseTolerance * 2
  expr: Constraints[5] = <<P90Measurements>>.ButtOverallHeight - <<ProjectSettings>>.WallThickness * 2 - <<ProjectSettings>>.LooseTolerance
  expr: Constraints[11] = <<ProjectSettings>>.WallThickness * 2 + <<ProjectSettings>>.LooseTolerance
  sketch-geometry (6):
    g0: ArcOfCircle CenterX=1e-15 CenterY=26.1159 CenterZ=0 NormalX=0 NormalY=0 NormalZ=1 AngleXU=0 Radius=17.8159 StartAngle=3.14159 EndAngle=4.71239
    g1: LineSegment StartX=17.8159 StartY=26.1159 StartZ=0 EndX=17.8159 EndY=94.1023 EndZ=0
    g2: LineSegment StartX=-17.8159 StartY=26.1159 StartZ=0 EndX=-17.8159 EndY=94.1023 EndZ=0
    g3: ArcOfCircle CenterX=-4.4e-15 CenterY=94.1023 CenterZ=0 NormalX=0 NormalY=0 NormalZ=1 AngleXU=0 Radius=17.8159 StartAngle=1.5708 EndAngle=3.14159
    g4: ArcOfCircle CenterX=-4.4e-15 CenterY=94.1023 CenterZ=0 NormalX=0 NormalY=0 NormalZ=1 AngleXU=0 Radius=17.8159 StartAngle=0 EndAngle=1.5708
    g5: ArcOfCircle CenterX=1e-15 CenterY=26.1159 CenterZ=0 NormalX=0 NormalY=0 NormalZ=1 AngleXU=0 Radius=17.8159 StartAngle=4.71239 EndAngle=6.28319
  constraints (15):
    c: Vertical(g2)
    c: Vertical(g1)
    c: DistanceX(g2,g1) = 35.6318
    c: Tangent(g2,g3) = 1.5708
    c: Tangent(g1,g4) = -1.5708
    c: DistanceY(g-1,g3) = 111.918
    c: Tangent(g4,g3) = -1.5708
    c: PointOnObject(g3,g-2)
    c: Symmetric(g2,g1,g-2)
    c: Tangent(g1,g5) = -1.5708
    c: Tangent(g0,g2) = 1.5708
    c: DistanceY(g-1,g5) = 8.3
    c: Tangent(g0,g5) = -1.5708
    c: PointOnObject(g0,g-2)
    c: Horizontal(g0,g1)
FEATURE [PartDesign::Pad] Pad015  label="PaperworkLidMainPad"
  Direction = (1,1,1)
  Length = 1.5
  Length2 = 100
  Placement = pos=(0,0,0) rot=(1,0,0;1.5708rad)
  Profile = -> Sketch043
  Reversed = true
  Type = 0
  expr: Length = <<ProjectSettings>>.PaperworklidbaseThickness
FEATURE [Sketcher::SketchObject] Sketch044  label="PaperworkLidWallAndNubSketch"
  AttachmentOffset = pos=(0,0,60.1091) rot=(0,0,1;0rad)
  FullyConstrained = true
  MapMode = 5
  Placement = pos=(0,0,60.1091) rot=(0,0,1;0rad)
  Support = -> [XY_Plane011]
  expr: Constraints[8] = <<ProjectSettings>>.PaperworkLidNubWidth
  expr: Constraints[10] = <<LightningCutPocket>>.Length - <<ProjectSettings>>.LooseTolerance
  expr: Constraints[6] = (<<P90Measurements>>.PadWidestWidth - <<ProjectSettings>>.TelescopingPadComfortFilletRadius * 3 - <<ProjectSettings>>.LooseTolerance * 2) / 2
  expr: .AttachmentOffset.Base.z = <<P90Measurements>>.ButtOverallHeight / 2
  expr: Constraints[9] = <<ProjectSettings>>.PaperworkLidNubHeight
  expr: Constraints[14] = <<ProjectSettings>>.PaperworklidbaseThickness
  expr: Constraints[17] = <<ProjectSettings>>.PaperworkLidWallThickness
  expr: Constraints[19] = <<ProjectSettings>>.PaperworkLipTabWallFilletRadius
  expr: Constraints[20] = <<ProjectSettings>>.PaperwokLipInteriorWallAngle
  sketch-geometry (7):
    g0: LineSegment StartX=-17.8159 StartY=0 StartZ=0 EndX=-17.8159 EndY=9.7 EndZ=0
    g1: LineSegment StartX=-17.8159 StartY=9.7 StartZ=0 EndX=-19.3159 EndY=10.7 EndZ=0
    g2: LineSegment StartX=-19.3159 StartY=10.7 StartZ=0 EndX=-17.8159 EndY=11.7 EndZ=0
    g3: LineSegment StartX=-17.8159 StartY=11.7 StartZ=0 EndX=-15.8159 EndY=11.7 EndZ=0
    g4: ArcOfCircle CenterX=-9.30257 CenterY=5.5 CenterZ=0 NormalX=0 NormalY=0 NormalZ=1 AngleXU=0 Radius=4 StartAngle=3.49066 EndAngle=4.71239
    g5: LineSegment StartX=-13.0613 StartY=4.13192 StartZ=0 EndX=-15.8159 EndY=11.7 EndZ=0
    g6: LineSegment StartX=-17.8159 StartY=0 StartZ=0 EndX=-9.30257 EndY=1.5 EndZ=0
  constraints (21):
    c: PointOnObject(g0,g-1)
    c: Vertical(g0)
    c: Coincident(g0,g1)
    c: Coincident(g1,g2)
    c: Coincident(g2,g3)
    c: Horizontal(g3)
    c: DistanceX(g0,g-1) = 17.8159
    c: Equal(g1,g2)
    c: DistanceY(g0,g2) = 2
    c: DistanceX(g1,g0) = 1.5
    c: DistanceY(g-1,g3) = 11.7
    c: Vertical(g2,g0)
    c: Coincident(g5,g3)
    c: Tangent(g5,g4) = 1.5708
    c: DistanceY(g6,g4) = 1.5
    c: Vertical(g4,g4)
    c: Coincident(g6,g4)
    c: DistanceX(g3,g3) = 2
    c: Coincident(g6,g0)
    c: Radius(g4) = 4
    c: Angle(g3,g5) = 1.91986
FEATURE [PartDesign::AdditivePipe] AdditivePipe  label="PaperworkLidWallAndNubAdditivePipe"
  AuxilleryCurvelinear = true
  AuxillerySpineTangent = false
  BaseFeature = -> Pad015
  Binormal = (0,0,0)
  Mode = 0
  Placement = pos=(0,0,0) rot=(1,0,0;1.5708rad)
  Profile = -> Sketch044
  Spine = -> Pad015 [Edge17]
  SpineTangent = false
  Transformation = 0
  Transition = 0
FEATURE [PartDesign::Mirrored] Mirrored003  label="PaperworkLidWallAndNubMirrored"
  BaseFeature = -> AdditivePipe
  MirrorPlane = -> Sketch044 [V_Axis]
  Originals = -> [AdditivePipe]
  Placement = pos=(0,0,0) rot=(1,0,0;1.5708rad)
  Refine = true
FEATURE [Sketcher::SketchObject] Sketch045  label="PaperworkLidCrosspinSlotSketch"
  FullyConstrained = true
  MapMode = 5
  Placement = pos=(0,0,0) rot=(0.57735,0.57735,0.57735;2.0944rad)
  Support = -> [YZ_Plane011]
  expr: Constraints[14] = <<ProjectSettings>>.StandardFillet
  expr: Constraints[0] = <<P90Measurements>>.PadWidestWidthOuterShoulderDistanceFromReferencePoint + <<ProjectSettings>>.BarHeight / 2 + <<ProjectSettings>>.TightTolerance
  expr: Constraints[1] = <<TelescopingPadSettings>>.TelescopingBarInsertDepth / 2 + <<ProjectSettings>>.TightTolerance * 2
  expr: Constraints[2] = <<ProjectSettings>>.CrosspinWidth + <<ProjectSettings>>.LooseTolerance * 2
  expr: Constraints[8] = <<LightningCutPocket>>.Length
  sketch-geometry (10):
    g0: ArcOfCircle CenterX=5.8875 CenterY=78.339 CenterZ=0 NormalX=0 NormalY=0 NormalZ=1 AngleXU=0 Radius=2.3 StartAngle=1.5708 EndAngle=4.71239
    g1: LineSegment StartX=5.8875 StartY=80.639 StartZ=0 EndX=10 EndY=80.639 EndZ=0
    g2: LineSegment StartX=12 StartY=80.639 StartZ=0 EndX=12 EndY=76.039 EndZ=0
    g3: LineSegment StartX=10 StartY=76.039 StartZ=0 EndX=5.8875 EndY=76.039 EndZ=0
    g4: LineSegment StartX=12 StartY=80.639 StartZ=0 EndX=12 EndY=82.639 EndZ=0
    g5: ArcOfCircle CenterX=10 CenterY=82.639 CenterZ=0 NormalX=0 NormalY=0 NormalZ=1 AngleXU=0 Radius=2 StartAngle=4.71239 EndAngle=6.28319
    g6: GeomPoint X=12 Y=80.639 Z=0
    g7: LineSegment StartX=12 StartY=76.039 StartZ=0 EndX=12 EndY=74.039 EndZ=0
    g8: ArcOfCircle CenterX=10 CenterY=74.039 CenterZ=0 NormalX=0 NormalY=0 NormalZ=1 AngleXU=0 Radius=2 StartAngle=2.7e-15 EndAngle=1.5708
    g9: GeomPoint X=12 Y=76.039 Z=0
  constraints (25):
    c: DistanceY(g-1,g0) = 78.339
    c: DistanceX(g-1,g0) = 5.8875
    c: Diameter(g0) = 4.6
    c: Coincident(g6,g2)
    c: Coincident(g2,g9)
    c: Horizontal(g1)
    c: Horizontal(g3)
    c: Vertical(g2)
    c: DistanceX(g-1,g6) = 12
    c: Vertical(g3,g0)
    c: Coincident(g0,g1)
    c: Coincident(g0,g3)
    c: Vertical(g0,g0)
    c: Vertical(g4)
    c: DistanceY(g6,g4) = 2
    c: PointOnObject(g6,g1)
    c: Tangent(g1,g5) = -1.5708
    c: Coincident(g4,g2)
    c: Tangent(g5,g4) = -1.5708
    c: Vertical(g7)
    c: PointOnObject(g9,g3)
    c: Tangent(g3,g8) = -1.5708
    c: Coincident(g7,g2)
    c: Tangent(g8,g7) = 1.5708
    c: Equal(g8,g5)
FEATURE [PartDesign::Pocket] Pocket024  label="PaperworkLidCrosspinSlotPocket"
  BaseFeature = -> Mirrored003
  Length = 5
  Length2 = 100
  Midplane = true
  Placement = pos=(0,0,0) rot=(1,0,0;1.5708rad)
  Profile = -> Sketch045
  Type = 1
FEATURE [Sketcher::SketchObject] Sketch046  label="PaperworkLidFingerHoleSketch"
  AttachmentOffset = pos=(0,0,60.1091) rot=(0,0,1;0rad)
  FullyConstrained = false
  MapMode = 5
  Placement = pos=(0,0,60.1091) rot=(0,0,1;0rad)
  Support = -> [XY_Plane011]
  expr: Constraints[6] = <<ProjectSettings>>.PaperworklidbaseThickness
  expr: Constraints[7] = <<ProjectSettings>>.PaperworkLidFingerHoleDiameter / 2
  expr: .AttachmentOffset.Base.z = <<P90Measurements>>.ButtOverallHeight / 2
  sketch-geometry (7):
    g0: LineSegment StartX=0 StartY=0 StartZ=0 EndX=10 EndY=0 EndZ=0
    g1: LineSegment StartX=10 StartY=1.5 StartZ=0 EndX=0 EndY=1.5 EndZ=0
    g2: LineSegment StartX=0 StartY=1.5 StartZ=0 EndX=0 EndY=0 EndZ=0
    g3: ArcOfCircle CenterX=10 CenterY=0.75 CenterZ=0 NormalX=0 NormalY=0 NormalZ=1 AngleXU=0 Radius=0.75 StartAngle=1.5708 EndAngle=4.71239
    g4: LineSegment StartX=0 StartY=1.5 StartZ=0 EndX=0 EndY=8.15565 EndZ=0
    g5: LineSegment StartX=0 StartY=8.15565 StartZ=0 EndX=10 EndY=8.15565 EndZ=0
    g6: LineSegment StartX=10 StartY=8.15565 StartZ=0 EndX=10 EndY=1.5 EndZ=0
  constraints (19):
    c: Coincident(g1,g2)
    c: Coincident(g2,g0)
    c: Horizontal(g0)
    c: Horizontal(g1)
    c: Vertical(g2)
    c: Coincident(g0,g-1)
    c: DistanceY(g2,g2) = 1.5
    c: DistanceX(g1,g1) = 10
    c: Coincident(g3,g1)
    c: Coincident(g3,g0)
    c: Vertical(g3,g0)
    c: Vertical(g0,g1)
    c: Coincident(g1,g4)
    c: PointOnObject(g4,g-2)
    c: Coincident(g4,g5)
    c: Horizontal(g5)
    c: Coincident(g5,g6)
    c: Vertical(g6)
    c: Coincident(g6,g1)
FEATURE [PartDesign::Groove] Groove  label="PaperworkLidFingerHoleGroove"
  Angle = 360
  Axis = (0,1,0)
  Base = (0,0,60.1091)
  BaseFeature = -> Pocket024
  Placement = pos=(0,0,0) rot=(1,0,0;1.5708rad)
  Profile = -> Sketch046
  ReferenceAxis = -> Sketch046 [V_Axis]
FEATURE [PartDesign::Body] Body008  label="PaperworkLid"
  Group = -> [Sketch043,Pad015,Sketch044,AdditivePipe,Mirrored003,Sketch045,Pocket024,Sketch046,Groove]
  Origin = -> Origin011
  Placement = pos=(0,18,0) rot=(0,0,1;0rad)
  Tip = -> Groove
  expr: .Placement.Base.y = <<PadBodyPad>>.Length
FEATURE [PartDesign::Fillet] Fillet024  label="interior fillet"
  Base = -> Mirrored002 [Edge201,Edge25,Edge186]
  BaseFeature = -> Mirrored002
  Placement = pos=(0,0,0) rot=(1,0,0;1.5708rad)
  Radius = 1
  SupportTransform = false
FEATURE [PartDesign::Body] Body002  label="TelescopingPad"
  Group = -> [Sketch008,Pad006,Sketch009,Pocket002,Sketch010,Pad007,Sketch011,Mirrored,Pocket003,Fillet,Sketch029,Pocket014,Sketch040,Pocket022,LinearPattern,Sketch041,Pocket023,LinearPattern002,Fillet023,Sketch042,SubtractivePipe,Mirrored002,Fillet024]
  Origin = -> Origin002
  Placement = pos=(0,18,0) rot=(0,0,1;0rad)
  Tip = -> Fillet024
  expr: .Placement.Base.y = <<PadBodyPad>>.Length
FEATURE [Sketcher::SketchObject] Sketch047  label="BarEndcapSketch"
  FullyConstrained = true
  MapMode = 5
  Placement = pos=(0,-265,-5.88e-14) rot=(1,0,0;1.5708rad)
  Support = -> [Pocket012]
  expr: Constraints[5] = <<CentralPadTelescopingBarInsertArmSketch>>.Constraints.BarArmWallThickness
  expr: Constraints[2] = <<ProjectSettings>>.BarHeight
  expr: Constraints[6] = <<ProjectSettings>>.BarThickness / 2
  sketch-geometry (4):
    g0: ArcOfCircle CenterX=2.5 CenterY=2.93 CenterZ=0 NormalX=0 NormalY=0 NormalZ=1 AngleXU=0 Radius=4.57 StartAngle=0 EndAngle=1.5708
    g1: ArcOfCircle CenterX=2.5 CenterY=-2.93 CenterZ=0 NormalX=0 NormalY=0 NormalZ=1 AngleXU=0 Radius=4.57 StartAngle=4.71239 EndAngle=6.28319
    g2: LineSegment StartX=2.5 StartY=7.5 StartZ=0 EndX=2.5 EndY=-7.5 EndZ=0
    g3: LineSegment StartX=7.07 StartY=2.93 StartZ=0 EndX=7.07 EndY=-2.93 EndZ=0
  constraints (9):
    c: Tangent(g1,g3) = 1.5708
    c: Tangent(g3,g0) = 1.5708
    c: DistanceY(g2,g2) = 15
    c: Symmetric(g2,g2,g-1)
    c: Symmetric(g1,g0,g-1)
    c: DistanceX(g2,g0) = 4.57
    c: DistanceX(g-1,g2) = 2.5
    c: Perpendicular(g0,g2) = 1.5708
    c: Coincident(g1,g2)
FEATURE [PartDesign::Pad] Pad016  label="BarEndcapPad"
  BaseFeature = -> Pocket012
  Direction = (1,1,1)
  Length = 4.9
  Length2 = 100
  Placement = pos=(0,0,0) rot=(1,0,0;1.5708rad)
  Profile = -> Sketch047
  Reversed = true
  Type = 0
  expr: Length = <<ProjectSettings>>.BarThickness - <<ProjectSettings>>.TightTolerance
FEATURE [Sketcher::SketchObject] Sketch048  label="BarReinforcmentSketch"
  FullyConstrained = true
  MapMode = 5
  Placement = pos=(0,-260.1,0) rot=(-1,0,0;1.5708rad)
  Support = -> [Pad016]
  expr: Constraints[7] = <<CentralPadTelescopingBarInsertArmSketch>>.Constraints.BarArmWallThickness
  expr: Constraints[8] = <<ProjectSettings>>.BarHeight / 3
  expr: Constraints[9] = <<ProjectSettings>>.BarThickness / 2
  sketch-geometry (4):
    g0: LineSegment StartX=2.5 StartY=2.5 StartZ=0 EndX=7.07 EndY=2.5 EndZ=0
    g1: LineSegment StartX=7.07 StartY=2.5 StartZ=0 EndX=7.07 EndY=-2.5 EndZ=0
    g2: LineSegment StartX=7.07 StartY=-2.5 StartZ=0 EndX=2.5 EndY=-2.5 EndZ=0
    g3: LineSegment StartX=2.5 StartY=-2.5 StartZ=0 EndX=2.5 EndY=2.5 EndZ=0
  constraints (11):
    c: Coincident(g0,g1)
    c: Coincident(g1,g2)
    c: Coincident(g2,g3)
    c: Coincident(g3,g0)
    c: Horizontal(g0)
    c: Horizontal(g2)
    c: Vertical(g3)
    c: DistanceX(g0,g0) = 4.57
    c: DistanceY(g1,g1) = 5
    c: DistanceX(g-1,g2) = 2.5
    c: Symmetric(g0,g1,g-1)
FEATURE [PartDesign::Pad] Pad017  label="BarReinforcmentPad"
  BaseFeature = -> Pad016
  Direction = (1,1,1)
  Length = 247.9
  Length2 = 100
  Placement = pos=(0,0,0) rot=(1,0,0;1.5708rad)
  Profile = -> Sketch048
  Refine = true
  Type = 0
  expr: Length = <<ProjectSettings>>.BarLength - <<ProjectSettings>>.BarRackStartOffset + <<ProjectSettings>>.WallThickness - <<ProjectSettings>>.TightTolerance
FEATURE [PartDesign::Fillet] Fillet025  label="2mm fillet"
  Base = -> Pad017 [Edge100,Edge89,Edge77,Edge111,Edge122,Edge133,Edge144,Edge58,Edge2,Edge161,Edge178,Edge177]
  BaseFeature = -> Pad017
  Placement = pos=(0,0,0) rot=(1,0,0;1.5708rad)
  Radius = 2
  SupportTransform = false
FEATURE [Sketcher::SketchObject] Sketch049  label="LockingButtonOverhangCompensationSketch"
  AttachmentOffset = pos=(0,0,-4) rot=(0,0,1;0rad)
  FullyConstrained = true
  MapMode = 5
  Placement = pos=(0,4,9e-16) rot=(1,0,0;1.5708rad)
  Support = -> [XZ_Plane]
  expr: Constraints[7] = <<ProjectSettings>>.LockingButtonWidth + <<ProjectSettings>>.LooseTolerance * 2
  expr: .AttachmentOffset.Base.z = -1 * <<ProjectSettings>>.WallThickness
  expr: Constraints[8] = <<LockingButtonHolePocket>>.Length
  sketch-geometry (3):
    g0: LineSegment StartX=-5.3 StartY=111.914 StartZ=0 EndX=5.3 EndY=111.914 EndZ=0
    g1: LineSegment StartX=5.3 StartY=111.914 StartZ=0 EndX=0 EndY=117.214 EndZ=0
    g2: LineSegment StartX=0 StartY=117.214 StartZ=0 EndX=-5.3 EndY=111.914 EndZ=0
  constraints (9):
    c: Horizontal(g0)
    c: Coincident(g0,g1)
    c: PointOnObject(g1,g-2)
    c: Coincident(g1,g2)
    c: Coincident(g2,g0)
    c: Angle(g0,g2) = 0.785398
    c: Equal(g2,g1)
    c: DistanceX(g0,g0) = 10.6
    c: DistanceY(g-1,g0) = 111.914
FEATURE [PartDesign::Pocket] Pocket025  label="LockingButtonOverhangCompensationPocket"
  BaseFeature = -> Fillet017
  Length = 10.6
  Length2 = 100
  Placement = pos=(0,0,0) rot=(1,0,0;1.5708rad)
  Profile = -> Sketch049
  Type = 0
  expr: Length = <<ProjectSettings>>.LockingButtonHeight + <<ProjectSettings>>.LooseTolerance * 2
FEATURE [Sketcher::SketchObject] Sketch050  label="LockingPinHoleOverhangSketch"
  FullyConstrained = true
  MapMode = 5
  Placement = pos=(0,0,0) rot=(0.57735,0.57735,0.57735;2.0944rad)
  Support = -> [YZ_Plane]
  expr: Constraints[8] = <<ProjectSettings>>.LockingPinWidth + <<ProjectSettings>>.LooseTolerance * 2
  expr: Constraints[9] = <<P90Measurements>>.PadWidestWidthOuterShoulderDistanceFromReferencePoint + (<<TelescopingBarSettings>>.BarHeight - <<TelescopingBarSettings>>.LockingPinHeight) / 2
  expr: Constraints[10] = <<ProjectSettings>>.WallThickness
  expr: Constraints[11] = <<P90Measurements>>.PadWidestWidthOuterShoulderDistanceFromReferencePoint + <<TelescopingBarSettings>>.BarHeight + <<TelescopingBarSettings>>.LockingPinHeight + <<ProjectSettings>>.LooseTolerance * 2
  sketch-geometry (6):
    g0: LineSegment StartX=4 StartY=90.039 StartZ=0 EndX=9.3625 EndY=90.039 EndZ=0
    g1: LineSegment StartX=9.3625 StartY=90.039 StartZ=0 EndX=9.3625 EndY=74.089 EndZ=0
    g2: LineSegment StartX=9.3625 StartY=74.089 StartZ=0 EndX=4 EndY=74.089 EndZ=0
    g3: LineSegment StartX=4 StartY=74.089 StartZ=0 EndX=4 EndY=90.039 EndZ=0
    g4: LineSegment StartX=4 StartY=90.039 StartZ=0 EndX=6.68125 EndY=92.7202 EndZ=0
    g5: LineSegment StartX=6.68125 StartY=92.7202 StartZ=0 EndX=9.3625 EndY=90.039 EndZ=0
  constraints (17):
    c: Coincident(g0,g1)
    c: Coincident(g1,g2)
    c: Coincident(g2,g3)
    c: Coincident(g3,g0)
    c: Horizontal(g0)
    c: Horizontal(g2)
    c: Vertical(g1)
    c: Vertical(g3)
    c: DistanceX(g0,g0) = 5.3625
    c: DistanceY(g-1,g2) = 74.089
    c: DistanceX(g-1,g2) = 4
    c: DistanceY(g-1,g0) = 90.039
    c: Coincident(g0,g4)
    c: Coincident(g4,g5)
    c: Coincident(g5,g0)
    c: Equal(g4,g5)
    c: Angle(g0,g4) = 0.785398
FEATURE [PartDesign::Pocket] Pocket026  label="LockingPinHoleOverhangPocket"
  BaseFeature = -> Pocket025
  Length = 62.0468
  Length2 = 100
  Midplane = true
  Placement = pos=(0,0,0) rot=(1,0,0;1.5708rad)
  Profile = -> Sketch050
  Type = 0
  expr: Length = <<LockingPinHolePocket>>.Length
FEATURE [PartDesign::Body] Body  label="LockingBody"
  Group = -> [Sketch,Pad,Sketch001,Pad001,Sketch002,Pocket,Sketch003,Pad002,Sketch004,Pocket001,Sketch014,Pad008,Mirrored001,Sketch018,Pocket007,Sketch019,Pocket008,Sketch022,Pocket010,Fillet016,Fillet017,Sketch049,Pocket025,Sketch050,Pocket026]
  Origin = -> Origin
  Tip = -> Pocket026
FEATURE [Sketcher::SketchObject] Sketch052  label="CrosspinMainBodySketch"
  FullyConstrained = true
  MapMode = 5
  Placement = pos=(0,0,0) rot=(0.57735,0.57735,0.57735;2.0944rad)
  Support = -> [YZ_Plane012]
  expr: Constraints[19] = <<ProjectSettings>>.CrosspinWidth - <<ProjectSettings>>.TightTolerance * 2
  sketch-geometry (7):
    g0: LineSegment StartX=-1.9 StartY=0 StartZ=0 EndX=-0.95 EndY=-1.64545 EndZ=0
    g1: LineSegment StartX=-0.95 StartY=-1.64545 StartZ=0 EndX=0.95 EndY=-1.64545 EndZ=0
    g2: LineSegment StartX=0.95 StartY=-1.64545 StartZ=0 EndX=1.9 EndY=-2e-16 EndZ=0
    g3: LineSegment StartX=1.9 StartY=-2e-16 StartZ=0 EndX=0.95 EndY=1.64545 EndZ=0
    g4: LineSegment StartX=0.95 StartY=1.64545 StartZ=0 EndX=-0.95 EndY=1.64545 EndZ=0
    g5: LineSegment StartX=-0.95 StartY=1.64545 StartZ=0 EndX=-1.9 EndY=0 EndZ=0
    g6: Circle CenterX=0 CenterY=0 CenterZ=0 NormalX=0 NormalY=0 NormalZ=1 AngleXU=0 Radius=1.9
  constraints (16):
    c: Coincident(g0,g1)
    c: Coincident(g1,g2)
    c: Coincident(g2,g3)
    c: Coincident(g3,g4)
    c: Coincident(g4,g5)
    c: Coincident(g5,g0)
    c: Equal(g0, g1-g5) x5
    c: PointOnObject(g0,g6)
    c: PointOnObject(g1,g6)
    c: PointOnObject(g2,g6)
    c: PointOnObject(g3,g6)
    c: PointOnObject(g4,g6)
    c: PointOnObject(g5,g6)
    c: Coincident(g6,g-1)
    c: PointOnObject(g5,g-1)
    c: DistanceX(g0,g2) = 3.8
FEATURE [PartDesign::Pad] Pad018  label="CrosspinMainBodyPad"
  Direction = (1,1,1)
  Length = 17
  Length2 = 100
  Placement = pos=(0,0,0) rot=(0.57735,0.57735,0.57735;2.0944rad)
  Profile = -> Sketch052
  Type = 0
  expr: Length = <<ProjectSettings>>.PadCrosspinLength
FEATURE [PartDesign::Chamfer] Chamfer  label="InserttionChamfer"
  Angle = 45
  Base = -> Pad018 [Face7]
  BaseFeature = -> Pad018
  ChamferType = 0
  FlipDirection = false
  Placement = pos=(0,0,0) rot=(0.57735,0.57735,0.57735;2.0944rad)
  Size = 1
  Size2 = 1
  SupportTransform = false
FEATURE [PartDesign::Body] Body009  label="PadCrosspin"
  Group = -> [Sketch052,Pad018,Chamfer]
  Origin = -> Origin012
  Placement = pos=(18,23.8875,78.339) rot=(0,0,1;0rad)
  Tip = -> Chamfer
  expr: .Placement.Base.z = <<P90Measurements>>.PadWidestWidthOuterShoulderDistanceFromReferencePoint + <<ProjectSettings>>.BarHeight / 2 + <<ProjectSettings>>.TightTolerance
  expr: .Placement.Base.y = <<TelescopingPadSettings>>.TelescopingBarInsertDepth / 2 + <<ProjectSettings>>.TightTolerance * 2 + <<ProjectSettings>>.LockingBodyPadThickness
FEATURE [PartDesign::Fillet] Fillet026  label="1point5mmfillet"
  Base = -> Fillet025 [Edge224,Edge68,Edge210,Edge63,Edge13,Edge25,Edge37,Edge49,Edge46,Edge34,Edge22,Edge10,Edge8]
  BaseFeature = -> Fillet025
  Placement = pos=(0,0,0) rot=(1,0,0;1.5708rad)
  Radius = 1.5
  SupportTransform = false
FEATURE [PartDesign::Body] Body006  label="RightTelescopingBar"
  Group = -> [Sketch025,Pad013,Sketch024,Pocket011,Sketch027,Pocket013,LinearPattern001,Sketch028,Pocket012,Sketch047,Pad016,Sketch048,Pad017,Fillet025,Fillet026]
  Origin = -> Origin007
  Placement = pos=(-28.4159,30,78.289) rot=(0,1,0;3.14159rad)
  Tip = -> Fillet026
  expr: .Placement.Base.y = <<ProjectSettings>>.WallThickness * 4 + <<ProjectSettings>>.LockingButtonWidth + <<ProjectSettings>>.CrosspinWidth
  expr: .Placement.Base.x = -1 * (<<P90Measurements>>.PadWidestWidth / 2 + <<ProjectSettings>>.BarThickness / 2) - <<ProjectSettings>>.LooseTolerance
  expr: .Placement.Base.z = <<P90Measurements>>.PadWidestWidthOuterShoulderDistanceFromReferencePoint + <<ProjectSettings>>.BarHeight / 2 + <<ProjectSettings>>.TightTolerance / 2
FEATURE [Part::Mirroring] Part__Mirroring  label="LeftTelescopingBar"
  Base = (7.62939e-06,-102.5,78.339)
  Normal = (1,0,-1.19209e-07)
  Source = -> Body006
FEATURE [PartDesign::Fillet] Fillet027
  Base = -> Fillet004 [Edge3]
  BaseFeature = -> Fillet004
  Placement = pos=(0,0,0) rot=(0.57735,0.57735,0.57735;2.0944rad)
  Radius = 1
  SupportTransform = false
FEATURE [PartDesign::Body] Body004  label="LockingPin"
  Group = -> [Sketch017,Pad010,Fillet004,Fillet027]
  Origin = -> Origin005
  Placement = pos=(0,6.48125,80.139) rot=(0,0,1;0rad)
  Tip = -> Fillet027
  expr: .Placement.Base.z = <<P90Measurements>>.PadWidestWidthOuterShoulderDistanceFromReferencePoint + <<TelescopingBarSettings>>.BarHeight - <<TelescopingBarSettings>>.LockingPinHeight / 2 - <<ProjectSettings>>.LooseTolerance
  expr: .Placement.Base.y = <<ProjectSettings>>.WallThickness + <<ProjectSettings>>.LockingPinWidth / 2 + <<ProjectSettings>>.TightTolerance
FEATURE [App::Part] Part002  label="LockingMechanism"
  Group = -> [Body005,Body004]
  Origin = -> Origin009
  Placement = pos=(0,0,6.5) rot=(0,0,1;0rad)
FEATURE [Sketcher::SketchObject] Sketch053  label="LockingBodySupportBaseSketch"
  FullyConstrained = true
  MapMode = 5
  Placement = pos=(0,0,0) rot=(1,0,0;1.5708rad)
  Support = -> [XZ_Plane013]
  expr: Constraints[22] = <<P90Measurements>>.PadWidestWidth
  expr: Constraints[23] = <<P90Measurements>>.PadThinnestWidth
  expr: Constraints[25] = <<P90Measurements>>.PadBottomWidth
  expr: Constraints[24] = <<P90Measurements>>.PadWidestWidthInnerShoulderDistanceFromReferencePoint - 5mm
  expr: Constraints[20] = <<P90Measurements>>.ButtOverallHeight
  sketch-geometry (17):
    g0: ArcOfCircle CenterX=-3.81 CenterY=18.6944 CenterZ=0 NormalX=0 NormalY=0 NormalZ=1 AngleXU=0 Radius=18.6944 StartAngle=3.14159 EndAngle=4.71239
    g1: ArcOfCircle CenterX=3.81 CenterY=18.6944 CenterZ=0 NormalX=0 NormalY=0 NormalZ=1 AngleXU=0 Radius=18.6944 StartAngle=4.71239 EndAngle=6.28319
    g2: ArcOfCircle CenterX=-5e-16 CenterY=94.6023 CenterZ=0 NormalX=0 NormalY=0 NormalZ=1 AngleXU=0 Radius=25.6159 StartAngle=1.5708 EndAngle=3.14159
    g3: ArcOfCircle CenterX=-5e-16 CenterY=94.6023 CenterZ=0 NormalX=0 NormalY=0 NormalZ=1 AngleXU=0 Radius=25.6159 StartAngle=0 EndAngle=1.5708
    g4: LineSegment StartX=-25.6159 StartY=94.6023 StartZ=0 EndX=-25.6159 EndY=59.3128 EndZ=0
    g5: LineSegment StartX=-25.6159 StartY=59.3128 StartZ=0 EndX=-22.5044 EndY=59.3128 EndZ=0
    g6: LineSegment StartX=-22.5044 StartY=59.3128 StartZ=0 EndX=-22.5044 EndY=18.6944 EndZ=0
    g7: LineSegment StartX=-3.81 StartY=0 StartZ=0 EndX=3.81 EndY=0 EndZ=0
    g8: LineSegment StartX=22.5044 StartY=18.6944 StartZ=0 EndX=22.5044 EndY=59.3128 EndZ=0
    g9: LineSegment StartX=22.5044 StartY=59.3128 StartZ=0 EndX=25.6159 EndY=59.3128 EndZ=0
    g10: LineSegment StartX=25.6159 StartY=59.3128 StartZ=0 EndX=25.6159 EndY=94.6023 EndZ=0
    g11: LineSegment StartX=-22.5044 StartY=18.6944 StartZ=0 EndX=-25.6159 EndY=18.6944 EndZ=0
    g12: LineSegment StartX=22.5044 StartY=18.6944 StartZ=0 EndX=25.6159 EndY=18.6944 EndZ=0
    g13: LineSegment StartX=-25.6159 StartY=0 StartZ=0 EndX=-25.6159 EndY=18.6944 EndZ=0
    g14: LineSegment StartX=25.6159 StartY=18.6944 StartZ=0 EndX=25.6159 EndY=0 EndZ=0
    g15: LineSegment StartX=-3.81 StartY=0 StartZ=0 EndX=-25.6159 EndY=0 EndZ=0
    g16: LineSegment StartX=3.81 StartY=0 StartZ=0 EndX=25.6159 EndY=0 EndZ=0
  constraints (43):
    c: Symmetric(g13,g14,g-2)
    c: PointOnObject(g0,g-1)
    c: PointOnObject(g1,g-1)
    c: Vertical(g4)
    c: Coincident(g5,g4)
    c: Vertical(g6)
    c: Vertical(g8)
    c: Coincident(g9,g8)
    c: Vertical(g10)
    c: Coincident(g9,g10)
    c: Horizontal(g9)
    c: Tangent(g2,g4) = -1.5708
    c: Tangent(g3,g10) = -1.5708
    c: Tangent(g6,g0) = -1.5708
    c: Tangent(g7,g0) = -1.5708
    c: Tangent(g7,g1) = -1.5708
    c: Tangent(g8,g1) = -1.5708
    c: Symmetric(g8,g6,g-2)
    c: Symmetric(g4,g9,g-2)
    c: Coincident(g6,g5)
    c: DistanceY(g-1,g3) = 120.218
    c: Equal(g1,g0)
    c: DistanceX(g2,g3) = 51.2318
    c: DistanceX(g5,g8) = 45.0088
    c: DistanceY(g-1,g8) = 59.3128
    c: DistanceX(g7,g7) = 7.62
    c: PointOnObject(g2,g-2)
    c: Tangent(g2,g3) = -1.5708
    c: Equal(g4,g10)
    c: Coincident(g11,g0)
    c: Horizontal(g11)
    c: Coincident(g12,g1)
    c: Horizontal(g12)
    c: Vertical(g13)
    c: Coincident(g13,g11)
    c: Coincident(g14,g12)
    c: Vertical(g14)
    c: Vertical(g12,g9)
    c: Coincident(g15,g0)
    c: Coincident(g15,g13)
    c: Horizontal(g15)
    c: Coincident(g16,g1)
    c: Coincident(g16,g14)
FEATURE [PartDesign::Pad] Pad019
  Direction = (1,1,1)
  Length = 18
  Length2 = 100
  Placement = pos=(0,0,0) rot=(1,0,0;1.5708rad)
  Profile = -> Sketch053
  Reversed = true
  Type = 0
  expr: Length = <<PadBodyPad>>.Length
FEATURE [PartDesign::Body] Body010  label="LockingBodySupport"
  Group = -> [Sketch053,Pad019]
  Origin = -> Origin013
  Placement = pos=(-0.16,0,0) rot=(0,0,1;0rad)
  Tip = -> Pad019
  expr: .Placement.Base.x = -1 * <<ProjectSettings>>.SupportGap
FEATURE [Part::Mirroring] Part__Mirroring001  label="LockingBodySupport Mirror"
  Base = (0,0,0)
  Normal = (1,0,0)
  Source = -> Body010
FEATURE [App::Part] Part001  label="LockingAssembly"
  Group = -> [Body,Part002,Body010,Part__Mirroring001]
  Origin = -> Origin008
  Placement = pos=(0,205,0) rot=(0,0,1;0rad)
FEATURE [Sketcher::SketchObject] Sketch054
  FullyConstrained = true
  MapMode = 5
  Placement = pos=(0,0,0) rot=(1,0,0;1.5708rad)
  Support = -> [XZ_Plane014]
  expr: Constraints[10] = <<ProjectSettings>>.BCGWidth
  expr: Constraints[9] = <<ProjectSettings>>.BcgEndHeight
  sketch-geometry (5):
    g0: LineSegment StartX=-21.25 StartY=7.5 StartZ=0 EndX=21.25 EndY=7.5 EndZ=0
    g1: LineSegment StartX=21.25 StartY=7.5 StartZ=0 EndX=21.25 EndY=-7.5 EndZ=0
    g2: LineSegment StartX=21.25 StartY=-7.5 StartZ=0 EndX=-21.25 EndY=-7.5 EndZ=0
    g3: LineSegment StartX=-21.25 StartY=-7.5 StartZ=0 EndX=-21.25 EndY=7.5 EndZ=0
    g4: Circle CenterX=0 CenterY=0 CenterZ=0 NormalX=0 NormalY=0 NormalZ=1 AngleXU=0 Radius=3.5
  constraints (12):
    c: Coincident(g0,g1)
    c: Coincident(g1,g2)
    c: Coincident(g2,g3)
    c: Coincident(g3,g0)
    c: Horizontal(g2)
    c: Vertical(g1)
    c: Coincident(g4,g-1)
    c: Symmetric(g0,g0,g-2)
    c: Symmetric(g2,g0,g-1)
    c: DistanceY(g3,g3) = 15
    c: DistanceX(g0,g0) = 42.5
    c: Diameter(g4) = 7
FEATURE [PartDesign::Pad] Pad020
  Direction = (1,1,1)
  Length = 5
  Length2 = 100
  Placement = pos=(0,0,0) rot=(1,0,0;1.5708rad)
  Profile = -> Sketch054
  Type = 0
  expr: Length = <<ProjectSettings>>.BCGInsertOffset
FEATURE [PartDesign::Body] Body011  label="BcgSpacer"
  Group = -> [Sketch054,Pad020]
  Origin = -> Origin014
  Tip = -> Pad020
FEATURE [App::Part] Part  label="TelescopingArray"
  Group = -> [Body002,Body008,Body006,Part__Mirroring,Body009,Body011]
  Origin = -> Origin003
  Placement = pos=(0,205,0) rot=(0,0,1;0rad)
